FREECAD ASSEMBLY — COMPONENT RECIPES ("surge_platform")

This assembly document has 21 components, labeled P0..P20 below (a component is one placed body or linked part). 10 of them carry a construction recipe — the FreeCAD feature program that regenerates the part from scratch, quoted from this document or its linked companion documents; the rest are supplied as boundary geometry only. No exploded tour is included for this assembly.
COMPONENT P0 — geometry summary ("BK12"; no construction recipe available for this part):
  bounding box: 60.0 x 43.0 x 35.0 mm
  tessellated surface: 281,450 triangles
  volume: 48234 mm^3 (53% of its bounding box)
COMPONENT P1 — geometry summary ("SFU1605_ball_screw_250mm"; no construction recipe available for this part):
  bounding box: 250.0 x 16.0 x 16.0 mm
  tessellated surface: 247,790 triangles
  volume: 33080 mm^3 (52% of its bounding box)
  symmetry: revolution-symmetric about the y axis through its bounding-box center
COMPONENT P2 — geometry summary ("SHF25_001"; no construction recipe available for this part):
  bounding box: 70.0 x 42.0 x 25.0 mm
  tessellated surface: 2,866 triangles
  volume: 24549 mm^3 (33% of its bounding box)
  symmetry: mirror-symmetric across its x mid-plane
COMPONENT P3 — geometry summary ("SHF25_002"; no construction recipe available for this part):
  bounding box: 70.0 x 42.0 x 25.0 mm
  tessellated surface: 2,866 triangles
  volume: 24549 mm^3 (33% of its bounding box)
  symmetry: mirror-symmetric across its x mid-plane
COMPONENT P4 — geometry summary ("SHF25_003"; no construction recipe available for this part):
  bounding box: 70.0 x 42.0 x 25.0 mm
  tessellated surface: 2,866 triangles
  volume: 24549 mm^3 (33% of its bounding box)
  symmetry: mirror-symmetric across its x mid-plane
COMPONENT P5 — geometry summary ("SHF25_000"; no construction recipe available for this part):
  bounding box: 70.0 x 42.0 x 25.0 mm
  tessellated surface: 2,866 triangles
  volume: 24549 mm^3 (33% of its bounding box)
  symmetry: mirror-symmetric across its x mid-plane
COMPONENT P6 — geometry summary ("80ST-M02438"; no construction recipe available for this part):
  bounding box: 185.6 x 92.0 x 80.0 mm
  tessellated surface: 23,724 triangles
  volume: 810178 mm^3 (59% of its bounding box)
COMPONENT P7 — geometry summary ("corner_bracket_40x40_001"; no construction recipe available for this part):
  bounding box: 38.5 x 38.5 x 36.0 mm
  tessellated surface: 328 triangles
  volume: 17428 mm^3 (33% of its bounding box)
  symmetry: mirror-symmetric across its x mid-plane
COMPONENT P8 — geometry summary ("corner_bracket_40x40_002"; no construction recipe available for this part):
  bounding box: 38.5 x 38.5 x 36.0 mm
  tessellated surface: 328 triangles
  volume: 17428 mm^3 (33% of its bounding box)
  symmetry: mirror-symmetric across its x mid-plane
COMPONENT P9 — geometry summary ("corner_bracket_40x40_003"; no construction recipe available for this part):
  bounding box: 38.5 x 38.5 x 36.0 mm
  tessellated surface: 328 triangles
  volume: 17428 mm^3 (33% of its bounding box)
  symmetry: mirror-symmetric across its x mid-plane
COMPONENT P10 — geometry summary ("corner_bracket_40x40_000"; no construction recipe available for this part):
  bounding box: 38.5 x 38.5 x 36.0 mm
  tessellated surface: 328 triangles
  volume: 17428 mm^3 (33% of its bounding box)
  symmetry: mirror-symmetric across its x mid-plane
COMPONENT P11 — recipe-attached ("coupler_10x19", a linked part whose construction recipe lives in a companion FreeCAD document of the same project; that document's serialized recipe follows).
Construction recipe (the companion document, serialized — sketch geometry with constraints, then the solid features built on it; lengths are millimeters unless a unit is written):

FCSTD DOCUMENT  (FreeCAD 1.0R39109 (Git))
Label: coupler
License: All rights reserved
LicenseURL: https://en.wikipedia.org/wiki/All_rights_reserved
objects: Sketcher::SketchObject×3, PartDesign::Pocket×2, PartDesign::Pad×1, PartDesign::Body×1
note: 16 computed .brp shape members not serialized (recipe doc carries the construction recipe); baked Part::Feature solids carry a one-line shape summary decoded from their .brp

FEATURE [Sketcher::SketchObject] Sketch
  ArcFitTolerance = 1e-06
  AttachmentSupport = -> [XZ_Plane]
  FullyConstrained = true
  MakeInternals = false
  MapMode = 5
  Placement = pos=(0,0,0) rot=(1,0,0;1.5708rad)
  sketch-geometry (1):
    g0: Circle CenterX=0 CenterY=0 CenterZ=0 NormalX=0 NormalY=0 NormalZ=1 AngleXU=0 Radius=17.5
  constraints (2):
    c: Coincident(g0,g-1)
    c: Diameter(g0) = 35
FEATURE [PartDesign::Pad] Pad
  Direction = (0,-1,2e-16)
  Length = 50
  Length2 = 10
  Placement = pos=(0,0,0) rot=(1,0,0;1.5708rad)
  Profile = -> Sketch
  ReferenceAxis = -> Sketch [N_Axis]
  Refine = true
  Suppressed = false
  Type = 0
FEATURE [Sketcher::SketchObject] Sketch001
  ArcFitTolerance = 1e-06
  AttachmentSupport = -> [Pad]
  FullyConstrained = true
  MakeInternals = false
  MapMode = 5
  Placement = pos=(0,-50,0) rot=(1,0,0;1.5708rad)
  sketch-geometry (1):
    g0: Circle CenterX=0 CenterY=0 CenterZ=0 NormalX=0 NormalY=0 NormalZ=1 AngleXU=0 Radius=9.5
  constraints (2):
    c: Coincident(g0,g-1)
    c: Diameter(g0) = 19
FEATURE [PartDesign::Pocket] Pocket
  BaseFeature = -> Pad
  Direction = (0,1,-2e-16)
  Length = 18.5
  Length2 = 5
  Placement = pos=(0,0,0) rot=(1,0,0;1.5708rad)
  Profile = -> Sketch001
  ReferenceAxis = -> Sketch001 [N_Axis]
  Refine = true
  Suppressed = false
  Type = 0
FEATURE [Sketcher::SketchObject] Sketch002
  ArcFitTolerance = 1e-06
  AttachmentSupport = -> [Pocket]
  FullyConstrained = true
  MakeInternals = false
  MapMode = 5
  Placement = pos=(0,0,0) rot=(-1,0,0;1.5708rad)
  sketch-geometry (1):
    g0: Circle CenterX=0 CenterY=0 CenterZ=0 NormalX=0 NormalY=0 NormalZ=1 AngleXU=0 Radius=5
  constraints (2):
    c: Diameter(g0) = 10
    c: Coincident(g0,g-1)
FEATURE [PartDesign::Pocket] Pocket001
  BaseFeature = -> Pocket
  Direction = (0,-1,-2e-16)
  Length = 18.5
  Length2 = 5
  Placement = pos=(0,0,0) rot=(1,0,0;1.5708rad)
  Profile = -> Sketch002
  ReferenceAxis = -> Sketch002 [N_Axis]
  Refine = true
  Suppressed = false
  Type = 0
FEATURE [PartDesign::Body] Body  label="coupler_10x19"
  AllowCompound = false
  Group = -> [Sketch,Pad,Sketch001,Pocket,Sketch002,Pocket001]
  Origin = -> Origin
  Tip = -> Pocket001
COMPONENT P12 — recipe-attached ("linear_shaft_25x500_right", a linked part whose construction recipe lives in a companion FreeCAD document of the same project; that document's serialized recipe follows).
Construction recipe (the companion document, serialized — sketch geometry with constraints, then the solid features built on it; lengths are millimeters unless a unit is written):

FCSTD DOCUMENT  (FreeCAD 1.0R39109 (Git))
Label: linear_shaft
License: All rights reserved
LicenseURL: https://en.wikipedia.org/wiki/All_rights_reserved
objects: Sketcher::SketchObject×2, PartDesign::Pad×2, PartDesign::Body×2
note: 12 computed .brp shape members not serialized (recipe doc carries the construction recipe); baked Part::Feature solids carry a one-line shape summary decoded from their .brp

FEATURE [Sketcher::SketchObject] Sketch
  ArcFitTolerance = 1e-06
  AttachmentSupport = -> [XZ_Plane]
  FullyConstrained = true
  MakeInternals = false
  MapMode = 5
  Placement = pos=(0,0,0) rot=(1,0,0;1.5708rad)
  sketch-geometry (1):
    g0: Circle CenterX=0 CenterY=0 CenterZ=0 NormalX=0 NormalY=0 NormalZ=1 AngleXU=0 Radius=12.5
  constraints (2):
    c: Diameter(g0) = 25
    c: Coincident(g0,g-1)
FEATURE [PartDesign::Pad] Pad
  Direction = (0,-1,2e-16)
  Length = 500
  Length2 = 10
  Placement = pos=(0,0,0) rot=(1,0,0;1.5708rad)
  Profile = -> Sketch
  ReferenceAxis = -> Sketch [N_Axis]
  Refine = true
  Suppressed = false
  Type = 0
FEATURE [PartDesign::Body] Body  label="linear_shaft_25x500"
  AllowCompound = false
  Group = -> [Sketch,Pad]
  Origin = -> Origin
  Tip = -> Pad
FEATURE [Sketcher::SketchObject] Sketch001
  ArcFitTolerance = 1e-06
  AttachmentSupport = -> [XZ_Plane001]
  FullyConstrained = true
  MakeInternals = false
  MapMode = 5
  Placement = pos=(0,0,0) rot=(1,0,0;1.5708rad)
  sketch-geometry (1):
    g0: Circle CenterX=0 CenterY=0 CenterZ=0 NormalX=0 NormalY=0 NormalZ=1 AngleXU=0 Radius=12.5
  constraints (2):
    c: Diameter(g0) = 25
    c: Coincident(g0,g-1)
FEATURE [PartDesign::Pad] Pad001
  Direction = (0,-1,2e-16)
  Length = 428
  Length2 = 10
  Placement = pos=(0,0,0) rot=(1,0,0;1.5708rad)
  Profile = -> Sketch001
  ReferenceAxis = -> Sketch001 [N_Axis]
  Refine = true
  Suppressed = false
  Type = 0
FEATURE [PartDesign::Body] Body001  label="linear_shaft_25x428"
  AllowCompound = false
  Group = -> [Sketch001,Pad001]
  Origin = -> Origin001
  Tip = -> Pad001
COMPONENT P13 — same part as P12; its construction recipe is shown at P12.
COMPONENT P14 — recipe-attached ("profile_40x40x500_right", a linked part whose construction recipe lives in a companion FreeCAD document of the same project; that document's serialized recipe follows).
Construction recipe (the companion document, serialized — sketch geometry with constraints, then the solid features built on it; lengths are millimeters unless a unit is written):

FCSTD DOCUMENT  (FreeCAD 1.0R39109 (Git))
Label: profile_40_serie
License: All rights reserved
LicenseURL: https://en.wikipedia.org/wiki/All_rights_reserved
objects: PartDesign::FeatureBase×6, PartDesign::Body×6, PartDesign::Pad×4, Part::Feature×3, PartDesign::Pocket×2
note: 39 computed .brp shape members not serialized (recipe doc carries the construction recipe); baked Part::Feature solids carry a one-line shape summary decoded from their .brp

FEATURE [Part::Feature] Part__Feature  label="profile_40x160x1000"
  shape: bbox 160 x 40 x 1000 mm, 262 faces (baked)
FEATURE [Part::Feature] Part__Feature003  label="profile_40x40x300"
  shape: bbox 40 x 40 x 300 mm, 147 faces (baked)
FEATURE [PartDesign::FeatureBase] BaseFeature
  BaseFeature = -> Part__Feature003
  Suppressed = false
FEATURE [PartDesign::Pad] Pad
  BaseFeature = -> BaseFeature
  Direction = (0,0,1)
  Length = 10
  Length2 = 10
  Profile = -> BaseFeature [Face147]
  Refine = true
  Suppressed = false
  Type = 0
FEATURE [PartDesign::Body] Body  label="profile_40x40x310"
  AllowCompound = false
  BaseFeature = -> Part__Feature003
  Group = -> [BaseFeature,Pad]
  Origin = -> Origin
  Tip = -> Pad
FEATURE [PartDesign::FeatureBase] BaseFeature001
  BaseFeature = -> Part__Feature
  Suppressed = false
FEATURE [PartDesign::Pad] Pad001
  BaseFeature = -> BaseFeature001
  Direction = (0,0,1)
  Length = 350
  Length2 = 10
  Profile = -> BaseFeature001 [Face9]
  Refine = true
  Suppressed = false
  Type = 0
FEATURE [PartDesign::Body] Body001  label="profile_40x160x1350"
  AllowCompound = false
  BaseFeature = -> Part__Feature
  Group = -> [BaseFeature001,Pad001]
  Origin = -> Origin001
  Tip = -> Pad001
FEATURE [PartDesign::FeatureBase] BaseFeature002
  BaseFeature = -> Part__Feature
  Suppressed = false
FEATURE [PartDesign::Pocket] Pocket
  BaseFeature = -> BaseFeature002
  Direction = (0,0,-1)
  Length = 500
  Length2 = 5
  Profile = -> BaseFeature002 [Face9]
  Refine = true
  Suppressed = false
  Type = 0
FEATURE [PartDesign::Body] Body002  label="profile_40x160x500"
  AllowCompound = false
  BaseFeature = -> Part__Feature
  Group = -> [BaseFeature002,Pocket]
  Origin = -> Origin002
  Tip = -> Pocket
FEATURE [PartDesign::FeatureBase] BaseFeature003
  BaseFeature = -> Part__Feature003
  Suppressed = false
FEATURE [PartDesign::Pad] Pad002
  BaseFeature = -> BaseFeature003
  Direction = (0,0,1)
  Length = 200
  Length2 = 10
  Profile = -> BaseFeature003 [Face147]
  Refine = true
  Suppressed = false
  Type = 0
FEATURE [PartDesign::Body] Body003  label="profile_40x40x500"
  AllowCompound = false
  BaseFeature = -> Part__Feature003
  Group = -> [BaseFeature003,Pad002]
  Origin = -> Origin003
  Tip = -> Pad002
FEATURE [Part::Feature] Part__Feature004  label="profile_40x120x80"
  shape: bbox 80 x 120 x 40 mm, 396 faces (baked)
FEATURE [PartDesign::FeatureBase] BaseFeature004
  BaseFeature = -> Part__Feature004
  Suppressed = false
FEATURE [PartDesign::Pad] Pad003
  BaseFeature = -> BaseFeature004
  Direction = (1,0,0)
  Length = 700
  Length2 = 10
  Profile = -> BaseFeature004 [Face396]
  Refine = true
  Suppressed = false
  Type = 0
FEATURE [PartDesign::Body] Body004  label="profile_40x120x780"
  AllowCompound = false
  BaseFeature = -> Part__Feature004
  Group = -> [BaseFeature004,Pad003]
  Origin = -> Origin004
  Tip = -> Pad003
FEATURE [PartDesign::FeatureBase] BaseFeature005
  BaseFeature = -> Part__Feature003
  Suppressed = false
FEATURE [PartDesign::Pocket] Pocket001
  BaseFeature = -> BaseFeature005
  Direction = (0,0,-1)
  Length = 30
  Length2 = 5
  Profile = -> BaseFeature005 [Face147]
  Refine = true
  Suppressed = false
  Type = 0
FEATURE [PartDesign::Body] Body005  label="profile_40x40x270"
  AllowCompound = false
  BaseFeature = -> Part__Feature003
  Group = -> [BaseFeature005,Pocket001]
  Origin = -> Origin005
  Tip = -> Pocket001
COMPONENT P15 — same part as P14; its construction recipe is shown at P14.
COMPONENT P16 — recipe-attached ("surge_BK12_mount_bottom", a linked part whose construction recipe lives in a companion FreeCAD document of the same project; that document's serialized recipe follows).
Construction recipe (the companion document, serialized — sketch geometry with constraints, then the solid features built on it; lengths are millimeters unless a unit is written):

FCSTD DOCUMENT  (FreeCAD 1.0R39109 (Git))
Label: surge_BK12_mount_bottom
License: All rights reserved
LicenseURL: https://en.wikipedia.org/wiki/All_rights_reserved
objects: Sketcher::SketchObject×5, PartDesign::Pocket×4, PartDesign::Fillet×2, PartDesign::Pad×1, PartDesign::Body×1
note: 32 computed .brp shape members not serialized (recipe doc carries the construction recipe); baked Part::Feature solids carry a one-line shape summary decoded from their .brp

FEATURE [Sketcher::SketchObject] Sketch
  ArcFitTolerance = 1e-06
  AttachmentSupport = -> [XZ_Plane]
  FullyConstrained = true
  MakeInternals = false
  MapMode = 5
  Placement = pos=(0,0,0) rot=(1,0,0;1.5708rad)
  sketch-geometry (28):
    g0: LineSegment [constr] StartX=-80 StartY=20 StartZ=0 EndX=-80 EndY=-20 EndZ=0
    g1: LineSegment [constr] StartX=-80 StartY=-20 StartZ=0 EndX=-40 EndY=-20 EndZ=0
    g2: LineSegment [constr] StartX=-40 StartY=-20 StartZ=0 EndX=-40 EndY=20 EndZ=0
    g3: LineSegment [constr] StartX=-40 StartY=20 StartZ=0 EndX=-80 EndY=20 EndZ=0
    g4: LineSegment [constr] StartX=40 StartY=20 StartZ=0 EndX=40 EndY=-20 EndZ=0
    g5: LineSegment [constr] StartX=40 StartY=-20 StartZ=0 EndX=80 EndY=-20 EndZ=0
    g6: LineSegment [constr] StartX=80 StartY=-20 StartZ=0 EndX=80 EndY=20 EndZ=0
    g7: LineSegment [constr] StartX=80 StartY=20 StartZ=0 EndX=40 EndY=20 EndZ=0
    g8: LineSegment [constr] StartX=-40 StartY=-20 StartZ=0 EndX=0 EndY=0 EndZ=0
    g9: LineSegment [constr] StartX=0 StartY=0 StartZ=0 EndX=40 EndY=-20 EndZ=0
    g10: LineSegment [constr] StartX=-30 StartY=-20.5 StartZ=0 EndX=30 EndY=-20.5 EndZ=0
    g11: LineSegment [constr] StartX=30 StartY=-20.5 StartZ=0 EndX=30 EndY=12 EndZ=0
    g12: LineSegment [constr] StartX=-30 StartY=-20.5 StartZ=0 EndX=-30 EndY=12 EndZ=0
    g13: LineSegment [constr] StartX=-30 StartY=12 StartZ=0 EndX=-17 EndY=12 EndZ=0
    g14: LineSegment [constr] StartX=-17 StartY=12 StartZ=0 EndX=-17 EndY=22.5 EndZ=0
    g15: LineSegment [constr] StartX=-17 StartY=22.5 StartZ=0 EndX=17 EndY=22.5 EndZ=0
    g16: LineSegment [constr] StartX=17 StartY=22.5 StartZ=0 EndX=17 EndY=12 EndZ=0
    g17: LineSegment [constr] StartX=17 StartY=12 StartZ=0 EndX=30 EndY=12 EndZ=0
    g18: LineSegment [constr] StartX=-30 StartY=-20.5 StartZ=0 EndX=0 EndY=0 EndZ=0
    g19: LineSegment [constr] StartX=0 StartY=0 StartZ=0 EndX=30 EndY=-20.5 EndZ=0
    g20: LineSegment StartX=-72.5 StartY=-30.4 StartZ=0 EndX=72.5 EndY=-30.4 EndZ=0
    g21: LineSegment StartX=30.4 StartY=-20.9 StartZ=0 EndX=-30.4 EndY=-20.9 EndZ=0
    g22: LineSegment StartX=72.5 StartY=-30.4 StartZ=0 EndX=72.5 EndY=-20.4 EndZ=0
    g23: LineSegment StartX=72.5 StartY=-20.4 StartZ=0 EndX=39.6 EndY=-20.4 EndZ=0
    g24: LineSegment StartX=-72.5 StartY=-30.4 StartZ=0 EndX=-72.5 EndY=-20.4 EndZ=0
    g25: LineSegment StartX=-72.5 StartY=-20.4 StartZ=0 EndX=-39.6 EndY=-20.4 EndZ=0
    g26: LineSegment StartX=-39.6 StartY=-20.4 StartZ=0 EndX=-30.4 EndY=-20.9 EndZ=0
    g27: LineSegment StartX=30.4 StartY=-20.9 StartZ=0 EndX=39.6 EndY=-20.4 EndZ=0
  constraints (80):
    c: Coincident(g0,g1)
    c: Coincident(g1,g2)
    c: Coincident(g2,g3)
    c: Coincident(g3,g0)
    c: Vertical(g0)
    c: Vertical(g2)
    c: Horizontal(g1)
    c: Horizontal(g3)
    c: Coincident(g4,g5)
    c: Coincident(g5,g6)
    c: Coincident(g6,g7)
    c: Coincident(g7,g4)
    c: Vertical(g4)
    c: Vertical(g6)
    c: Horizontal(g5)
    c: Horizontal(g7)
    c: Equal(g4,g7)
    c: Equal(g7,g2)
    c: Equal(g2,g3)
    c: DistanceX(g3,g3) = 40
    c: DistanceX(g2,g4) = 80
    c: DistanceY(g4,g2) = 0
    c: Coincident(g8,g1)
    c: Coincident(g8,g-1)
    c: Coincident(g9,g8)
    c: Coincident(g9,g4)
    c: Equal(g8,g9)
    c: Horizontal(g10)
    c: Coincident(g11,g10)
    c: Vertical(g11)
    c: Coincident(g12,g10)
    c: Vertical(g12)
    c: Coincident(g13,g12)
    c: Horizontal(g13)
    c: Coincident(g14,g13)
    c: Vertical(g14)
    c: Coincident(g15,g14)
    c: Horizontal(g15)
    c: Vertical(g16)
    c: Coincident(g17,g16)
    c: Coincident(g17,g11)
    c: DistanceX(g10,g10) = 60
    c: DistanceY(g12,g12) = 32.5
    c: Coincident(g16,g15)
    c: Horizontal(g17)
    c: Equal(g12,g11)
    c: Equal(g13,g17)
    c: DistanceX(g13,g13) = 13
    c: DistanceY(g14,g14) = 10.5
    c: DistanceY(g12,g2) = 8
    c: Coincident(g18,g10)
    c: Coincident(g18,g8)
    c: Coincident(g19,g8)
    c: Coincident(g19,g10)
    c: Equal(g19,g18)
    c: DistanceY(g8,g2) = 20
    c: Horizontal(g20)
    c: Horizontal(g21)
    c: DistanceY(g21,g10) = 0.4
    c: DistanceX(g21,g10) = 0.4
    c: DistanceX(g10,g21) = 0.4
    c: Coincident(g20,g22)
    c: Vertical(g22)
    c: Coincident(g22,g23)
    c: Horizontal(g23)
    c: Coincident(g20,g24)
    c: Vertical(g24)
    c: Coincident(g24,g25)
    c: Horizontal(g25)
    c: DistanceY(g24,g0) = 0.4
    c: DistanceY(g24,g24) = 10
    c: DistanceX(g1,g25) = 0.4
    c: Equal(g24,g22)
    c: DistanceX(g0,g24) = 7.5
    c: DistanceX(g23,g4) = 0.4
    c: Coincident(g26,g25)
    c: Coincident(g26,g21)
    c: Coincident(g27,g21)
    c: Coincident(g27,g23)
    c: DistanceX(g20,g20) = 145
FEATURE [PartDesign::Pad] Pad
  Direction = (0,-1,2e-16)
  Length = 25
  Length2 = 10
  Placement = pos=(0,0,0) rot=(1,0,0;1.5708rad)
  Profile = -> Sketch
  ReferenceAxis = -> Sketch [N_Axis]
  Refine = true
  Suppressed = false
  Type = 0
FEATURE [Sketcher::SketchObject] Sketch001
  ArcFitTolerance = 1e-06
  AttachmentSupport = -> [Pad]
  FullyConstrained = true
  MakeInternals = false
  MapMode = 5
  Placement = pos=(0,-4.5e-15,-20.4) rot=(0,0,1;3.14159rad)
  sketch-geometry (14):
    g0: LineSegment [constr] StartX=-80 StartY=0 StartZ=0 EndX=-40 EndY=0 EndZ=0
    g1: LineSegment [constr] StartX=-40 StartY=0 StartZ=0 EndX=-40 EndY=25 EndZ=0
    g2: LineSegment [constr] StartX=-40 StartY=25 StartZ=0 EndX=-80 EndY=25 EndZ=0
    g3: LineSegment [constr] StartX=-80 StartY=25 StartZ=0 EndX=-80 EndY=0 EndZ=0
    g4: LineSegment [constr] StartX=80 StartY=0 StartZ=0 EndX=80 EndY=25 EndZ=0
    g5: LineSegment [constr] StartX=80 StartY=25 StartZ=0 EndX=40 EndY=25 EndZ=0
    g6: LineSegment [constr] StartX=40 StartY=25 StartZ=0 EndX=40 EndY=0 EndZ=0
    g7: LineSegment [constr] StartX=40 StartY=0 StartZ=0 EndX=80 EndY=0 EndZ=0
    g8: LineSegment [constr] StartX=-80 StartY=0 StartZ=0 EndX=-40 EndY=25 EndZ=0
    g9: LineSegment [constr] StartX=-40 StartY=0 StartZ=0 EndX=-80 EndY=25 EndZ=0
    g10: LineSegment [constr] StartX=40 StartY=0 StartZ=0 EndX=80 EndY=25 EndZ=0
    g11: LineSegment [constr] StartX=40 StartY=25 StartZ=0 EndX=80 EndY=0 EndZ=0
    g12: Circle CenterX=-60 CenterY=12.5 CenterZ=0 NormalX=0 NormalY=0 NormalZ=1 AngleXU=0 Radius=4.3
    g13: Circle CenterX=60 CenterY=12.5 CenterZ=0 NormalX=0 NormalY=0 NormalZ=1 AngleXU=0 Radius=4.3
  constraints (36):
    c: Coincident(g0,g1)
    c: Coincident(g1,g2)
    c: Coincident(g2,g3)
    c: Coincident(g3,g0)
    c: Horizontal(g0)
    c: Horizontal(g2)
    c: Vertical(g1)
    c: Vertical(g3)
    c: Distance(g1,g3) = 40
    c: Distance(g0,g2) = 25
    c: PointOnObject(g0,g-1)
    c: Coincident(g4,g5)
    c: Coincident(g5,g6)
    c: Coincident(g6,g7)
    c: Coincident(g7,g4)
    c: Vertical(g4)
    c: Vertical(g6)
    c: Horizontal(g5)
    c: Horizontal(g7)
    c: PointOnObject(g4,g-1)
    c: Equal(g0,g7)
    c: Equal(g3,g4)
    c: DistanceX(g0,g-1) = 80
    c: DistanceX(g-1,g4) = 80
    c: Coincident(g8,g0)
    c: Coincident(g8,g1)
    c: Coincident(g9,g0)
    c: Coincident(g9,g2)
    c: Coincident(g10,g6)
    c: Coincident(g10,g4)
    c: Coincident(g11,g5)
    c: Coincident(g11,g4)
    c: Symmetric(g9,g9,g12)
    c: Diameter(g12) = 8.6
    c: Symmetric(g10,g10,g13)
    c: Equal(g13,g12)
FEATURE [PartDesign::Pocket] Pocket
  BaseFeature = -> Pad
  Direction = (0,0,-1)
  Length = 5
  Length2 = 5
  Placement = pos=(0,0,0) rot=(1,0,0;1.5708rad)
  Profile = -> Sketch001
  ReferenceAxis = -> Sketch001 [N_Axis]
  Refine = true
  Suppressed = false
  Type = 1
FEATURE [Sketcher::SketchObject] Sketch002
  ArcFitTolerance = 1e-06
  AttachmentSupport = -> [Pocket]
  FullyConstrained = true
  MakeInternals = false
  MapMode = 5
  Placement = pos=(0,-4.6e-15,-20.9) rot=(0,0,1;3.14159rad)
  sketch-geometry (7):
    g0: Circle CenterX=-23 CenterY=6 CenterZ=0 NormalX=0 NormalY=0 NormalZ=1 AngleXU=0 Radius=3.3
    g1: Circle CenterX=-23 CenterY=19 CenterZ=0 NormalX=0 NormalY=0 NormalZ=1 AngleXU=0 Radius=3.3
    g2: Circle CenterX=23 CenterY=19 CenterZ=0 NormalX=0 NormalY=0 NormalZ=1 AngleXU=0 Radius=3.3
    g3: Circle CenterX=23 CenterY=6 CenterZ=0 NormalX=0 NormalY=0 NormalZ=1 AngleXU=0 Radius=3.3
    g4: LineSegment [constr] StartX=-23 StartY=19 StartZ=0 EndX=23 EndY=6 EndZ=0
    g5: LineSegment [constr] StartX=23 StartY=19 StartZ=0 EndX=-23 EndY=6 EndZ=0
    g6: LineSegment [constr] StartX=0 StartY=0 StartZ=0 EndX=0 EndY=12.5 EndZ=0
  constraints (18):
    c: Diameter(g1) = 6.6
    c: Equal(g1,g0)
    c: Equal(g0,g3)
    c: Equal(g3,g2)
    c: DistanceY(g0,g1) = 13
    c: DistanceX(g1,g0) = 0
    c: DistanceY(g1,g2) = 0
    c: DistanceX(g3,g2) = 0
    c: DistanceY(g3,g0) = 0
    c: DistanceX(g1,g2) = 46
    c: Coincident(g4,g1)
    c: Coincident(g4,g3)
    c: Coincident(g5,g2)
    c: Coincident(g5,g0)
    c: Coincident(g6,g-1)
    c: Symmetric(g4,g4,g6)
    c: Vertical(g6)
    c: DistanceY(g6,g6) = 12.5
FEATURE [PartDesign::Pocket] Pocket001
  BaseFeature = -> Pocket
  Direction = (0,0,-1)
  Length = 5
  Length2 = 5
  Placement = pos=(0,0,0) rot=(1,0,0;1.5708rad)
  Profile = -> Sketch002
  ReferenceAxis = -> Sketch002 [N_Axis]
  Refine = true
  Suppressed = false
  Type = 1
FEATURE [PartDesign::Fillet] Fillet
  Base = -> Pocket001 [Edge13,Edge12,Edge20,Edge14]
  BaseFeature = -> Pocket001
  Placement = pos=(0,0,0) rot=(1,0,0;1.5708rad)
  Radius = 4
  Refine = true
  SupportTransform = false
  Suppressed = false
  UseAllEdges = false
FEATURE [PartDesign::Fillet] Fillet001
  Base = -> Fillet [Edge51,Edge52]
  BaseFeature = -> Fillet
  Placement = pos=(0,0,0) rot=(1,0,0;1.5708rad)
  Radius = 2
  Refine = true
  SupportTransform = false
  Suppressed = false
  UseAllEdges = false
FEATURE [Sketcher::SketchObject] Sketch004
  ArcFitTolerance = 1e-06
  AttachmentOffset = pos=(0,0,-10) rot=(0,0,1;0rad)
  AttachmentSupport = -> [Fillet001]
  FullyConstrained = true
  MakeInternals = false
  MapMode = 5
  Placement = pos=(0,-4.5e-15,-30.4) rot=(0,0,1;3.14159rad)
  sketch-geometry (16):
    g0: LineSegment [constr] StartX=-80 StartY=0 StartZ=0 EndX=-40 EndY=0 EndZ=0
    g1: LineSegment [constr] StartX=-40 StartY=0 StartZ=0 EndX=-40 EndY=25 EndZ=0
    g2: LineSegment [constr] StartX=-40 StartY=25 StartZ=0 EndX=-80 EndY=25 EndZ=0
    g3: LineSegment [constr] StartX=-80 StartY=25 StartZ=0 EndX=-80 EndY=0 EndZ=0
    g4: LineSegment [constr] StartX=80 StartY=0 StartZ=0 EndX=80 EndY=25 EndZ=0
    g5: LineSegment [constr] StartX=80 StartY=25 StartZ=0 EndX=40 EndY=25 EndZ=0
    g6: LineSegment [constr] StartX=40 StartY=25 StartZ=0 EndX=40 EndY=0 EndZ=0
    g7: LineSegment [constr] StartX=40 StartY=0 StartZ=0 EndX=80 EndY=0 EndZ=0
    g8: LineSegment [constr] StartX=-80 StartY=0 StartZ=0 EndX=-40 EndY=25 EndZ=0
    g9: LineSegment [constr] StartX=-40 StartY=0 StartZ=0 EndX=-80 EndY=25 EndZ=0
    g10: LineSegment [constr] StartX=40 StartY=0 StartZ=0 EndX=80 EndY=25 EndZ=0
    g11: LineSegment [constr] StartX=40 StartY=25 StartZ=0 EndX=80 EndY=0 EndZ=0
    g12: Circle [constr] CenterX=-60 CenterY=12.5 CenterZ=0 NormalX=0 NormalY=0 NormalZ=1 AngleXU=0 Radius=4.3
    g13: Circle [constr] CenterX=60 CenterY=12.5 CenterZ=0 NormalX=0 NormalY=0 NormalZ=1 AngleXU=0 Radius=4.3
    g14: Circle CenterX=-60 CenterY=12.5 CenterZ=0 NormalX=0 NormalY=0 NormalZ=1 AngleXU=0 Radius=6.75
    g15: Circle CenterX=60 CenterY=12.5 CenterZ=0 NormalX=0 NormalY=0 NormalZ=1 AngleXU=0 Radius=6.75
  constraints (40):
    c: Coincident(g0,g1)
    c: Coincident(g1,g2)
    c: Coincident(g2,g3)
    c: Coincident(g3,g0)
    c: Horizontal(g0)
    c: Horizontal(g2)
    c: Vertical(g1)
    c: Vertical(g3)
    c: Distance(g1,g3) = 40
    c: Distance(g0,g2) = 25
    c: PointOnObject(g0,g-1)
    c: Coincident(g4,g5)
    c: Coincident(g5,g6)
    c: Coincident(g6,g7)
    c: Coincident(g7,g4)
    c: Vertical(g4)
    c: Vertical(g6)
    c: Horizontal(g5)
    c: Horizontal(g7)
    c: PointOnObject(g4,g-1)
    c: Equal(g0,g7)
    c: Equal(g3,g4)
    c: DistanceX(g0,g-1) = 80
    c: DistanceX(g-1,g4) = 80
    c: Coincident(g8,g0)
    c: Coincident(g8,g1)
    c: Coincident(g9,g0)
    c: Coincident(g9,g2)
    c: Coincident(g10,g6)
    c: Coincident(g10,g4)
    c: Coincident(g11,g5)
    c: Coincident(g11,g4)
    c: Symmetric(g9,g9,g12)
    c: Diameter(g12) = 8.6
    c: Symmetric(g10,g10,g13)
    c: Equal(g13,g12)
    c: Diameter(g14) = 13.5
    c: Coincident(g14,g12)
    c: Coincident(g15,g13)
    c: Equal(g15,g14)
FEATURE [PartDesign::Pocket] Pocket003
  BaseFeature = -> Fillet001
  Direction = (0,0,-1)
  Length = 5
  Length2 = 5
  Placement = pos=(0,0,0) rot=(1,0,0;1.5708rad)
  Profile = -> Sketch004
  ReferenceAxis = -> Sketch004 [N_Axis]
  Refine = true
  Reversed = true
  Suppressed = false
  Type = 0
FEATURE [Sketcher::SketchObject] Sketch006
  ArcFitTolerance = 1e-06
  AttachmentOffset = pos=(0,0,-10) rot=(0,0,1;0rad)
  AttachmentSupport = -> [Pocket003]
  FullyConstrained = true
  MakeInternals = false
  MapMode = 5
  Placement = pos=(0,-4.5e-15,-30.4) rot=(0,0,1;3.14159rad)
  expr: Constraints[0] = Sketch002.Constraints[0]
  expr: Constraints[17] = Sketch002.Constraints[17]
  expr: Constraints[4] = Sketch002.Constraints[4]
  expr: Constraints[5] = Sketch002.Constraints[5]
  expr: Constraints[6] = Sketch002.Constraints[6]
  expr: Constraints[7] = Sketch002.Constraints[7]
  expr: Constraints[8] = Sketch002.Constraints[8]
  expr: Constraints[9] = Sketch002.Constraints[9]
  sketch-geometry (35):
    g0: Circle [constr] CenterX=-23 CenterY=6 CenterZ=0 NormalX=0 NormalY=0 NormalZ=1 AngleXU=0 Radius=3.3
    g1: Circle [constr] CenterX=-23 CenterY=19 CenterZ=0 NormalX=0 NormalY=0 NormalZ=1 AngleXU=0 Radius=3.3
    g2: Circle [constr] CenterX=23 CenterY=19 CenterZ=0 NormalX=0 NormalY=0 NormalZ=1 AngleXU=0 Radius=3.3
    g3: Circle [constr] CenterX=23 CenterY=6 CenterZ=0 NormalX=0 NormalY=0 NormalZ=1 AngleXU=0 Radius=3.3
    g4: LineSegment [constr] StartX=-23 StartY=19 StartZ=0 EndX=23 EndY=6 EndZ=0
    g5: LineSegment [constr] StartX=23 StartY=19 StartZ=0 EndX=-23 EndY=6 EndZ=0
    g6: LineSegment [constr] StartX=0 StartY=0 StartZ=0 EndX=0 EndY=12.5 EndZ=0
    g7: LineSegment StartX=-20.0266 StartY=13.85 StartZ=0 EndX=-17.0533 EndY=19 EndZ=0
    g8: LineSegment StartX=-17.0533 StartY=19 StartZ=0 EndX=-20.0266 EndY=24.15 EndZ=0
    g9: LineSegment StartX=-20.0266 StartY=24.15 StartZ=0 EndX=-25.9734 EndY=24.15 EndZ=0
    g10: LineSegment StartX=-25.9734 StartY=24.15 StartZ=0 EndX=-28.9467 EndY=19 EndZ=0
    g11: LineSegment StartX=-28.9467 StartY=19 StartZ=0 EndX=-25.9734 EndY=13.85 EndZ=0
    g12: LineSegment StartX=-25.9734 StartY=13.85 StartZ=0 EndX=-20.0266 EndY=13.85 EndZ=0
    g13: Circle [constr] CenterX=-23 CenterY=19 CenterZ=0 NormalX=0 NormalY=0 NormalZ=1 AngleXU=0 Radius=5.94671
    g14: LineSegment StartX=-20.0266 StartY=0.85 StartZ=0 EndX=-17.0533 EndY=6 EndZ=0
    g15: LineSegment StartX=-17.0533 StartY=6 StartZ=0 EndX=-20.0266 EndY=11.15 EndZ=0
    g16: LineSegment StartX=-20.0266 StartY=11.15 StartZ=0 EndX=-25.9734 EndY=11.15 EndZ=0
    g17: LineSegment StartX=-25.9734 StartY=11.15 StartZ=0 EndX=-28.9467 EndY=6 EndZ=0
    g18: LineSegment StartX=-28.9467 StartY=6 StartZ=0 EndX=-25.9734 EndY=0.85 EndZ=0
    g19: LineSegment StartX=-25.9734 StartY=0.85 StartZ=0 EndX=-20.0266 EndY=0.85 EndZ=0
    g20: Circle [constr] CenterX=-23 CenterY=6 CenterZ=0 NormalX=0 NormalY=0 NormalZ=1 AngleXU=0 Radius=5.94671
    g21: LineSegment StartX=25.9734 StartY=13.85 StartZ=0 EndX=28.9467 EndY=19 EndZ=0
    g22: LineSegment StartX=28.9467 StartY=19 StartZ=0 EndX=25.9734 EndY=24.15 EndZ=0
    g23: LineSegment StartX=25.9734 StartY=24.15 StartZ=0 EndX=20.0266 EndY=24.15 EndZ=0
    g24: LineSegment StartX=20.0266 StartY=24.15 StartZ=0 EndX=17.0533 EndY=19 EndZ=0
    g25: LineSegment StartX=17.0533 StartY=19 StartZ=0 EndX=20.0266 EndY=13.85 EndZ=0
    g26: LineSegment StartX=20.0266 StartY=13.85 StartZ=0 EndX=25.9734 EndY=13.85 EndZ=0
    g27: Circle [constr] CenterX=23 CenterY=19 CenterZ=0 NormalX=0 NormalY=0 NormalZ=1 AngleXU=0 Radius=5.94671
    g28: LineSegment StartX=25.9734 StartY=0.85 StartZ=0 EndX=28.9467 EndY=6 EndZ=0
    g29: LineSegment StartX=28.9467 StartY=6 StartZ=0 EndX=25.9734 EndY=11.15 EndZ=0
    g30: LineSegment StartX=25.9734 StartY=11.15 StartZ=0 EndX=20.0266 EndY=11.15 EndZ=0
    g31: LineSegment StartX=20.0266 StartY=11.15 StartZ=0 EndX=17.0533 EndY=6 EndZ=0
    g32: LineSegment StartX=17.0533 StartY=6 StartZ=0 EndX=20.0266 EndY=0.85 EndZ=0
    g33: LineSegment StartX=20.0266 StartY=0.85 StartZ=0 EndX=25.9734 EndY=0.85 EndZ=0
    g34: Circle [constr] CenterX=23 CenterY=6 CenterZ=0 NormalX=0 NormalY=0 NormalZ=1 AngleXU=0 Radius=5.94671
  constraints (82):
    c: Diameter(g1) = 6.6
    c: Equal(g1,g0)
    c: Equal(g0,g3)
    c: Equal(g3,g2)
    c: DistanceY(g0,g1) = 13
    c: DistanceX(g1,g0) = 0
    c: DistanceY(g1,g2) = 0
    c: DistanceX(g3,g2) = 0
    c: DistanceY(g3,g0) = 0
    c: DistanceX(g1,g2) = 46
    c: Coincident(g4,g1)
    c: Coincident(g4,g3)
    c: Coincident(g5,g2)
    c: Coincident(g5,g0)
    c: Coincident(g6,g-1)
    c: Symmetric(g4,g4,g6)
    c: Vertical(g6)
    c: DistanceY(g6,g6) = 12.5
    c: Coincident(g7,g8)
    c: Coincident(g8,g9)
    c: Coincident(g9,g10)
    c: Coincident(g10,g11)
    c: Coincident(g11,g12)
    c: Coincident(g12,g7)
    c: Equal(g7, g8-g12) x5
    c: PointOnObject(g7,g13)
    c: PointOnObject(g8,g13)
    c: PointOnObject(g9,g13)
    c: PointOnObject(g10,g13)
    c: PointOnObject(g11,g13)
    c: PointOnObject(g12,g13)
    c: Coincident(g13,g1)
    c: Coincident(g14,g15)
    c: Coincident(g15,g16)
    c: Coincident(g16,g17)
    c: Coincident(g17,g18)
    c: Coincident(g18,g19)
    c: Coincident(g19,g14)
    c: Equal(g14, g15-g19) x5
    c: PointOnObject(g14,g20)
    c: PointOnObject(g15,g20)
    c: PointOnObject(g16,g20)
    c: PointOnObject(g17,g20)
    c: PointOnObject(g18,g20)
    c: PointOnObject(g19,g20)
    c: Coincident(g20,g0)
    c: Coincident(g21,g22)
    c: Coincident(g22,g23)
    c: Coincident(g23,g24)
    c: Coincident(g24,g25)
    c: Coincident(g25,g26)
    c: Coincident(g26,g21)
    c: Equal(g21, g22-g26) x5
    c: PointOnObject(g21,g27)
    c: PointOnObject(g22,g27)
    c: PointOnObject(g23,g27)
    c: PointOnObject(g24,g27)
    c: PointOnObject(g25,g27)
    c: PointOnObject(g26,g27)
    c: Coincident(g27,g2)
    c: Coincident(g28,g29)
    c: Coincident(g29,g30)
    c: Coincident(g30,g31)
    c: Coincident(g31,g32)
    c: Coincident(g32,g33)
    c: Coincident(g33,g28)
    c: Equal(g28, g29-g33) x5
    c: PointOnObject(g28,g34)
    c: PointOnObject(g29,g34)
    c: PointOnObject(g30,g34)
    c: PointOnObject(g31,g34)
    c: PointOnObject(g32,g34)
    c: PointOnObject(g33,g34)
    c: Coincident(g34,g3)
    c: Horizontal(g9)
    c: Horizontal(g16)
    c: Horizontal(g23)
    c: Horizontal(g30)
    c: Distance(g9,g7) = 10.3
    c: Equal(g13,g20)
    c: Equal(g20,g34)
    c: Equal(g34,g27)
FEATURE [PartDesign::Pocket] Pocket005
  BaseFeature = -> Pocket003
  Direction = (0,0,-1)
  Length = 4
  Length2 = 5
  Placement = pos=(0,0,0) rot=(1,0,0;1.5708rad)
  Profile = -> Sketch006
  ReferenceAxis = -> Sketch006 [N_Axis]
  Refine = true
  Reversed = true
  Suppressed = false
  Type = 0
FEATURE [PartDesign::Body] Body  label="surge_BK12_mount_bottom"
  AllowCompound = false
  Group = -> [Sketch,Pad,Sketch001,Pocket,Sketch002,Pocket001,Fillet,Fillet001,Sketch004,Pocket003,Sketch006,Pocket005]
  Origin = -> Origin
  Tip = -> Pocket005
COMPONENT P17 — recipe-attached ("surge_BK12_mount_top", a linked part whose construction recipe lives in a companion FreeCAD document of the same project; that document's serialized recipe follows).
Construction recipe (the companion document, serialized — sketch geometry with constraints, then the solid features built on it; lengths are millimeters unless a unit is written):

FCSTD DOCUMENT  (FreeCAD 1.0R39109 (Git))
Label: surge_BK12_mount_top
License: All rights reserved
LicenseURL: https://en.wikipedia.org/wiki/All_rights_reserved
objects: Sketcher::SketchObject×5, PartDesign::Pocket×4, PartDesign::Fillet×2, PartDesign::Pad×1, PartDesign::Body×1
note: 32 computed .brp shape members not serialized (recipe doc carries the construction recipe); baked Part::Feature solids carry a one-line shape summary decoded from their .brp

FEATURE [Sketcher::SketchObject] Sketch
  ArcFitTolerance = 1e-06
  AttachmentSupport = -> [XZ_Plane]
  FullyConstrained = true
  MakeInternals = false
  MapMode = 5
  Placement = pos=(0,0,0) rot=(1,0,0;1.5708rad)
  sketch-geometry (32):
    g0: LineSegment [constr] StartX=-80 StartY=20 StartZ=0 EndX=-80 EndY=-20 EndZ=0
    g1: LineSegment [constr] StartX=-80 StartY=-20 StartZ=0 EndX=-40 EndY=-20 EndZ=0
    g2: LineSegment [constr] StartX=-40 StartY=-20 StartZ=0 EndX=-40 EndY=20 EndZ=0
    g3: LineSegment [constr] StartX=-40 StartY=20 StartZ=0 EndX=-80 EndY=20 EndZ=0
    g4: LineSegment [constr] StartX=40 StartY=20 StartZ=0 EndX=40 EndY=-20 EndZ=0
    g5: LineSegment [constr] StartX=40 StartY=-20 StartZ=0 EndX=80 EndY=-20 EndZ=0
    g6: LineSegment [constr] StartX=80 StartY=-20 StartZ=0 EndX=80 EndY=20 EndZ=0
    g7: LineSegment [constr] StartX=80 StartY=20 StartZ=0 EndX=40 EndY=20 EndZ=0
    g8: LineSegment [constr] StartX=-40 StartY=-20 StartZ=0 EndX=0 EndY=0 EndZ=0
    g9: LineSegment [constr] StartX=0 StartY=0 StartZ=0 EndX=40 EndY=-20 EndZ=0
    g10: LineSegment [constr] StartX=-30 StartY=-20.5 StartZ=0 EndX=30 EndY=-20.5 EndZ=0
    g11: LineSegment [constr] StartX=30 StartY=-20.5 StartZ=0 EndX=30 EndY=12 EndZ=0
    g12: LineSegment [constr] StartX=-30 StartY=-20.5 StartZ=0 EndX=-30 EndY=12 EndZ=0
    g13: LineSegment [constr] StartX=-30 StartY=12 StartZ=0 EndX=-17 EndY=12 EndZ=0
    g14: LineSegment [constr] StartX=-17 StartY=12 StartZ=0 EndX=-17 EndY=22.5 EndZ=0
    g15: LineSegment [constr] StartX=-17 StartY=22.5 StartZ=0 EndX=17 EndY=22.5 EndZ=0
    g16: LineSegment [constr] StartX=17 StartY=22.5 StartZ=0 EndX=17 EndY=12 EndZ=0
    g17: LineSegment [constr] StartX=17 StartY=12 StartZ=0 EndX=30 EndY=12 EndZ=0
    g18: LineSegment [constr] StartX=-30 StartY=-20.5 StartZ=0 EndX=0 EndY=0 EndZ=0
    g19: LineSegment [constr] StartX=0 StartY=0 StartZ=0 EndX=30 EndY=-20.5 EndZ=0
    g20: LineSegment StartX=72.5 StartY=30.4 StartZ=0 EndX=-72.5 EndY=30.4 EndZ=0
    g21: LineSegment StartX=-30 StartY=12.4 StartZ=0 EndX=-17.4 EndY=12.4 EndZ=0
    g22: LineSegment StartX=-17.4 StartY=12.4 StartZ=0 EndX=-17.4 EndY=22.9 EndZ=0
    g23: LineSegment StartX=-17.4 StartY=22.9 StartZ=0 EndX=17.4 EndY=22.9 EndZ=0
    g24: LineSegment StartX=17.4 StartY=22.9 StartZ=0 EndX=17.4 EndY=12.4 EndZ=0
    g25: LineSegment StartX=17.4 StartY=12.4 StartZ=0 EndX=30 EndY=12.4 EndZ=0
    g26: LineSegment StartX=39.6 StartY=20.4 StartZ=0 EndX=72.5 EndY=20.4 EndZ=0
    g27: LineSegment StartX=72.5 StartY=20.4 StartZ=0 EndX=72.5 EndY=30.4 EndZ=0
    g28: LineSegment StartX=-39.6 StartY=20.4 StartZ=0 EndX=-72.5 EndY=20.4 EndZ=0
    g29: LineSegment StartX=-72.5 StartY=20.4 StartZ=0 EndX=-72.5 EndY=30.4 EndZ=0
    g30: LineSegment StartX=-39.6 StartY=20.4 StartZ=0 EndX=-30 EndY=12.4 EndZ=0
    g31: LineSegment StartX=30 StartY=12.4 StartZ=0 EndX=39.6 EndY=20.4 EndZ=0
  constraints (92):
    c: Coincident(g0,g1)
    c: Coincident(g1,g2)
    c: Coincident(g2,g3)
    c: Coincident(g3,g0)
    c: Vertical(g0)
    c: Vertical(g2)
    c: Horizontal(g1)
    c: Horizontal(g3)
    c: Coincident(g4,g5)
    c: Coincident(g5,g6)
    c: Coincident(g6,g7)
    c: Coincident(g7,g4)
    c: Vertical(g4)
    c: Vertical(g6)
    c: Horizontal(g5)
    c: Horizontal(g7)
    c: Equal(g4,g7)
    c: Equal(g7,g2)
    c: Equal(g2,g3)
    c: DistanceX(g3,g3) = 40
    c: DistanceX(g2,g4) = 80
    c: DistanceY(g4,g2) = 0
    c: Coincident(g8,g1)
    c: Coincident(g8,g-1)
    c: Coincident(g9,g8)
    c: Coincident(g9,g4)
    c: Equal(g8,g9)
    c: Horizontal(g10)
    c: Coincident(g11,g10)
    c: Vertical(g11)
    c: Coincident(g12,g10)
    c: Vertical(g12)
    c: Coincident(g13,g12)
    c: Horizontal(g13)
    c: Coincident(g14,g13)
    c: Vertical(g14)
    c: Coincident(g15,g14)
    c: Horizontal(g15)
    c: Vertical(g16)
    c: Coincident(g17,g16)
    c: Coincident(g17,g11)
    c: DistanceX(g10,g10) = 60
    c: DistanceY(g12,g12) = 32.5
    c: Coincident(g16,g15)
    c: Horizontal(g17)
    c: Equal(g12,g11)
    c: Equal(g13,g17)
    c: DistanceX(g13,g13) = 13
    c: DistanceY(g14,g14) = 10.5
    c: DistanceY(g12,g2) = 8
    c: Coincident(g18,g10)
    c: Coincident(g18,g8)
    c: Coincident(g19,g8)
    c: Coincident(g19,g10)
    c: Equal(g19,g18)
    c: DistanceY(g8,g2) = 20
    c: Horizontal(g20)
    c: Horizontal(g21)
    c: Coincident(g21,g22)
    c: Vertical(g22)
    c: Coincident(g22,g23)
    c: Horizontal(g23)
    c: Coincident(g23,g24)
    c: Vertical(g24)
    c: Coincident(g24,g25)
    c: Horizontal(g25)
    c: Equal(g21,g25)
    c: DistanceY(g12,g21) = 0.4
    c: DistanceX(g21,g13) = 0.4
    c: DistanceY(g14,g22) = 0.4
    c: Horizontal(g26)
    c: Coincident(g26,g27)
    c: Coincident(g27,g20)
    c: Vertical(g27)
    c: Horizontal(g28)
    c: Coincident(g28,g29)
    c: Coincident(g29,g20)
    c: Vertical(g29)
    c: DistanceY(g2,g28) = 0.4
    c: Equal(g26,g28)
    c: DistanceX(g2,g28) = 0.4
    c: Coincident(g30,g28)
    c: Coincident(g30,g21)
    c: DistanceX(g20,g20) = 145
    c: DistanceY(g29,g29) = 10
    c: Equal(g27,g29)
    c: DistanceX(g26,g4) = 0.4
    c: Coincident(g31,g25)
    c: Coincident(g31,g26)
    c: DistanceX(g21,g12) = 0
    c: DistanceX(g15,g23) = 0.4
    c: Equal(g24,g22)
FEATURE [PartDesign::Pad] Pad
  Direction = (0,-1,2e-16)
  Length = 25
  Length2 = 10
  Placement = pos=(0,0,0) rot=(1,0,0;1.5708rad)
  Profile = -> Sketch
  ReferenceAxis = -> Sketch [N_Axis]
  Refine = true
  Suppressed = false
  Type = 0
FEATURE [Sketcher::SketchObject] Sketch001
  ArcFitTolerance = 1e-06
  AttachmentSupport = -> [Pad]
  FullyConstrained = true
  MakeInternals = false
  MapMode = 5
  Placement = pos=(0,6.8e-15,30.4) rot=(0,0,1;3.14159rad)
  sketch-geometry (14):
    g0: LineSegment [constr] StartX=-80 StartY=0 StartZ=0 EndX=-40 EndY=0 EndZ=0
    g1: LineSegment [constr] StartX=-40 StartY=0 StartZ=0 EndX=-40 EndY=25 EndZ=0
    g2: LineSegment [constr] StartX=-40 StartY=25 StartZ=0 EndX=-80 EndY=25 EndZ=0
    g3: LineSegment [constr] StartX=-80 StartY=25 StartZ=0 EndX=-80 EndY=0 EndZ=0
    g4: LineSegment [constr] StartX=80 StartY=0 StartZ=0 EndX=80 EndY=25 EndZ=0
    g5: LineSegment [constr] StartX=80 StartY=25 StartZ=0 EndX=40 EndY=25 EndZ=0
    g6: LineSegment [constr] StartX=40 StartY=25 StartZ=0 EndX=40 EndY=0 EndZ=0
    g7: LineSegment [constr] StartX=40 StartY=0 StartZ=0 EndX=80 EndY=0 EndZ=0
    g8: LineSegment [constr] StartX=-80 StartY=0 StartZ=0 EndX=-40 EndY=25 EndZ=0
    g9: LineSegment [constr] StartX=-40 StartY=0 StartZ=0 EndX=-80 EndY=25 EndZ=0
    g10: LineSegment [constr] StartX=40 StartY=0 StartZ=0 EndX=80 EndY=25 EndZ=0
    g11: LineSegment [constr] StartX=40 StartY=25 StartZ=0 EndX=80 EndY=0 EndZ=0
    g12: Circle CenterX=-60 CenterY=12.5 CenterZ=0 NormalX=0 NormalY=0 NormalZ=1 AngleXU=0 Radius=4.3
    g13: Circle CenterX=60 CenterY=12.5 CenterZ=0 NormalX=0 NormalY=0 NormalZ=1 AngleXU=0 Radius=4.3
  constraints (36):
    c: Coincident(g0,g1)
    c: Coincident(g1,g2)
    c: Coincident(g2,g3)
    c: Coincident(g3,g0)
    c: Horizontal(g0)
    c: Horizontal(g2)
    c: Vertical(g1)
    c: Vertical(g3)
    c: Distance(g1,g3) = 40
    c: Distance(g0,g2) = 25
    c: PointOnObject(g0,g-1)
    c: Coincident(g4,g5)
    c: Coincident(g5,g6)
    c: Coincident(g6,g7)
    c: Coincident(g7,g4)
    c: Vertical(g4)
    c: Vertical(g6)
    c: Horizontal(g5)
    c: Horizontal(g7)
    c: PointOnObject(g4,g-1)
    c: Equal(g0,g7)
    c: Equal(g3,g4)
    c: DistanceX(g0,g-1) = 80
    c: DistanceX(g-1,g4) = 80
    c: Coincident(g8,g0)
    c: Coincident(g8,g1)
    c: Coincident(g9,g0)
    c: Coincident(g9,g2)
    c: Coincident(g10,g6)
    c: Coincident(g10,g4)
    c: Coincident(g11,g5)
    c: Coincident(g11,g4)
    c: Symmetric(g9,g9,g12)
    c: Diameter(g12) = 8.6
    c: Symmetric(g10,g10,g13)
    c: Equal(g13,g12)
FEATURE [PartDesign::Pocket] Pocket
  BaseFeature = -> Pad
  Direction = (0,0,-1)
  Length = 5
  Length2 = 5
  Placement = pos=(0,0,0) rot=(1,0,0;1.5708rad)
  Profile = -> Sketch001
  ReferenceAxis = -> Sketch001 [N_Axis]
  Refine = true
  Suppressed = false
  Type = 1
FEATURE [Sketcher::SketchObject] Sketch002
  ArcFitTolerance = 1e-06
  AttachmentSupport = -> [Pocket]
  FullyConstrained = true
  MakeInternals = false
  MapMode = 5
  Placement = pos=(0,6.8e-15,30.4) rot=(0,0,1;3.14159rad)
  sketch-geometry (7):
    g0: Circle CenterX=-23 CenterY=6 CenterZ=0 NormalX=0 NormalY=0 NormalZ=1 AngleXU=0 Radius=3.3
    g1: Circle CenterX=-23 CenterY=19 CenterZ=0 NormalX=0 NormalY=0 NormalZ=1 AngleXU=0 Radius=3.3
    g2: Circle CenterX=23 CenterY=19 CenterZ=0 NormalX=0 NormalY=0 NormalZ=1 AngleXU=0 Radius=3.3
    g3: Circle CenterX=23 CenterY=6 CenterZ=0 NormalX=0 NormalY=0 NormalZ=1 AngleXU=0 Radius=3.3
    g4: LineSegment [constr] StartX=-23 StartY=19 StartZ=0 EndX=23 EndY=6 EndZ=0
    g5: LineSegment [constr] StartX=23 StartY=19 StartZ=0 EndX=-23 EndY=6 EndZ=0
    g6: LineSegment [constr] StartX=0 StartY=0 StartZ=0 EndX=0 EndY=12.5 EndZ=0
  constraints (18):
    c: Diameter(g1) = 6.6
    c: Equal(g1,g0)
    c: Equal(g0,g3)
    c: Equal(g3,g2)
    c: DistanceY(g0,g1) = 13
    c: DistanceX(g1,g0) = 0
    c: DistanceY(g1,g2) = 0
    c: DistanceX(g3,g2) = 0
    c: DistanceY(g3,g0) = 0
    c: DistanceX(g1,g2) = 46
    c: Coincident(g4,g1)
    c: Coincident(g4,g3)
    c: Coincident(g5,g2)
    c: Coincident(g5,g0)
    c: Coincident(g6,g-1)
    c: Symmetric(g4,g4,g6)
    c: Vertical(g6)
    c: DistanceY(g6,g6) = 12.5
FEATURE [PartDesign::Pocket] Pocket001
  BaseFeature = -> Pocket
  Direction = (0,0,-1)
  Length = 5
  Length2 = 5
  Placement = pos=(0,0,0) rot=(1,0,0;1.5708rad)
  Profile = -> Sketch002
  ReferenceAxis = -> Sketch002 [N_Axis]
  Refine = true
  Suppressed = false
  Type = 1
FEATURE [PartDesign::Fillet] Fillet
  Base = -> Pocket001 [Edge31,Edge22,Edge29,Edge20]
  BaseFeature = -> Pocket001
  Placement = pos=(0,0,0) rot=(1,0,0;1.5708rad)
  Radius = 4
  Refine = true
  SupportTransform = false
  Suppressed = false
  UseAllEdges = false
FEATURE [PartDesign::Fillet] Fillet001
  Base = -> Fillet [Edge39,Edge3]
  BaseFeature = -> Fillet
  Placement = pos=(0,0,0) rot=(1,0,0;1.5708rad)
  Radius = 2
  Refine = true
  SupportTransform = false
  Suppressed = false
  UseAllEdges = false
FEATURE [Sketcher::SketchObject] Sketch003
  ArcFitTolerance = 1e-06
  AttachmentSupport = -> [Fillet001]
  FullyConstrained = true
  MakeInternals = false
  MapMode = 5
  Placement = pos=(0,6.8e-15,30.4) rot=(0,0,1;3.14159rad)
  expr: Constraints[22] = Sketch001.Constraints[22]
  expr: Constraints[23] = Sketch001.Constraints[23]
  expr: Constraints[33] = Sketch001.Constraints[33]
  expr: Constraints[8] = Sketch001.Constraints[8]
  expr: Constraints[9] = Sketch001.Constraints[9]
  sketch-geometry (16):
    g0: LineSegment [constr] StartX=-80 StartY=0 StartZ=0 EndX=-40 EndY=0 EndZ=0
    g1: LineSegment [constr] StartX=-40 StartY=0 StartZ=0 EndX=-40 EndY=25 EndZ=0
    g2: LineSegment [constr] StartX=-40 StartY=25 StartZ=0 EndX=-80 EndY=25 EndZ=0
    g3: LineSegment [constr] StartX=-80 StartY=25 StartZ=0 EndX=-80 EndY=0 EndZ=0
    g4: LineSegment [constr] StartX=80 StartY=0 StartZ=0 EndX=80 EndY=25 EndZ=0
    g5: LineSegment [constr] StartX=80 StartY=25 StartZ=0 EndX=40 EndY=25 EndZ=0
    g6: LineSegment [constr] StartX=40 StartY=25 StartZ=0 EndX=40 EndY=0 EndZ=0
    g7: LineSegment [constr] StartX=40 StartY=0 StartZ=0 EndX=80 EndY=0 EndZ=0
    g8: LineSegment [constr] StartX=-80 StartY=0 StartZ=0 EndX=-40 EndY=25 EndZ=0
    g9: LineSegment [constr] StartX=-40 StartY=0 StartZ=0 EndX=-80 EndY=25 EndZ=0
    g10: LineSegment [constr] StartX=40 StartY=0 StartZ=0 EndX=80 EndY=25 EndZ=0
    g11: LineSegment [constr] StartX=40 StartY=25 StartZ=0 EndX=80 EndY=0 EndZ=0
    g12: Circle [constr] CenterX=-60 CenterY=12.5 CenterZ=0 NormalX=0 NormalY=0 NormalZ=1 AngleXU=0 Radius=4.3
    g13: Circle [constr] CenterX=60 CenterY=12.5 CenterZ=0 NormalX=0 NormalY=0 NormalZ=1 AngleXU=0 Radius=4.3
    g14: Circle CenterX=-60 CenterY=12.5 CenterZ=0 NormalX=0 NormalY=0 NormalZ=1 AngleXU=0 Radius=6.75
    g15: Circle CenterX=60 CenterY=12.5 CenterZ=0 NormalX=0 NormalY=0 NormalZ=1 AngleXU=0 Radius=6.75
  constraints (40):
    c: Coincident(g0,g1)
    c: Coincident(g1,g2)
    c: Coincident(g2,g3)
    c: Coincident(g3,g0)
    c: Horizontal(g0)
    c: Horizontal(g2)
    c: Vertical(g1)
    c: Vertical(g3)
    c: Distance(g1,g3) = 40
    c: Distance(g0,g2) = 25
    c: PointOnObject(g0,g-1)
    c: Coincident(g4,g5)
    c: Coincident(g5,g6)
    c: Coincident(g6,g7)
    c: Coincident(g7,g4)
    c: Vertical(g4)
    c: Vertical(g6)
    c: Horizontal(g5)
    c: Horizontal(g7)
    c: PointOnObject(g4,g-1)
    c: Equal(g0,g7)
    c: Equal(g3,g4)
    c: DistanceX(g0,g-1) = 80
    c: DistanceX(g-1,g4) = 80
    c: Coincident(g8,g0)
    c: Coincident(g8,g1)
    c: Coincident(g9,g0)
    c: Coincident(g9,g2)
    c: Coincident(g10,g6)
    c: Coincident(g10,g4)
    c: Coincident(g11,g5)
    c: Coincident(g11,g4)
    c: Symmetric(g9,g9,g12)
    c: Diameter(g12) = 8.6
    c: Symmetric(g10,g10,g13)
    c: Equal(g13,g12)
    c: Diameter(g14) = 13.5
    c: Coincident(g14,g12)
    c: Coincident(g15,g13)
    c: Equal(g15,g14)
FEATURE [PartDesign::Pocket] Pocket002
  BaseFeature = -> Fillet001
  Direction = (0,0,-1)
  Length = 5
  Length2 = 5
  Placement = pos=(0,0,0) rot=(1,0,0;1.5708rad)
  Profile = -> Sketch003
  ReferenceAxis = -> Sketch003 [N_Axis]
  Refine = true
  Suppressed = false
  Type = 0
FEATURE [Sketcher::SketchObject] Sketch005
  ArcFitTolerance = 1e-06
  AttachmentSupport = -> [Pocket002]
  FullyConstrained = true
  MakeInternals = false
  MapMode = 5
  Placement = pos=(0,6.8e-15,30.4) rot=(0,0,1;3.14159rad)
  expr: Constraints[0] = Sketch002.Constraints[0]
  expr: Constraints[17] = Sketch002.Constraints[17]
  expr: Constraints[4] = Sketch002.Constraints[4]
  expr: Constraints[5] = Sketch002.Constraints[5]
  expr: Constraints[6] = Sketch002.Constraints[6]
  expr: Constraints[7] = Sketch002.Constraints[7]
  expr: Constraints[8] = Sketch002.Constraints[8]
  expr: Constraints[9] = Sketch002.Constraints[9]
  sketch-geometry (11):
    g0: Circle [constr] CenterX=-23 CenterY=6 CenterZ=0 NormalX=0 NormalY=0 NormalZ=1 AngleXU=0 Radius=3.3
    g1: Circle [constr] CenterX=-23 CenterY=19 CenterZ=0 NormalX=0 NormalY=0 NormalZ=1 AngleXU=0 Radius=3.3
    g2: Circle [constr] CenterX=23 CenterY=19 CenterZ=0 NormalX=0 NormalY=0 NormalZ=1 AngleXU=0 Radius=3.3
    g3: Circle [constr] CenterX=23 CenterY=6 CenterZ=0 NormalX=0 NormalY=0 NormalZ=1 AngleXU=0 Radius=3.3
    g4: LineSegment [constr] StartX=-23 StartY=19 StartZ=0 EndX=23 EndY=6 EndZ=0
    g5: LineSegment [constr] StartX=23 StartY=19 StartZ=0 EndX=-23 EndY=6 EndZ=0
    g6: LineSegment [constr] StartX=0 StartY=0 StartZ=0 EndX=0 EndY=12.5 EndZ=0
    g7: Circle CenterX=-23 CenterY=19 CenterZ=0 NormalX=0 NormalY=0 NormalZ=1 AngleXU=0 Radius=5.25
    g8: Circle CenterX=-23 CenterY=6 CenterZ=0 NormalX=0 NormalY=0 NormalZ=1 AngleXU=0 Radius=5.25
    g9: Circle CenterX=23 CenterY=6 CenterZ=0 NormalX=0 NormalY=0 NormalZ=1 AngleXU=0 Radius=5.25
    g10: Circle CenterX=23 CenterY=19 CenterZ=0 NormalX=0 NormalY=0 NormalZ=1 AngleXU=0 Radius=5.25
  constraints (26):
    c: Diameter(g1) = 6.6
    c: Equal(g1,g0)
    c: Equal(g0,g3)
    c: Equal(g3,g2)
    c: DistanceY(g0,g1) = 13
    c: DistanceX(g1,g0) = 0
    c: DistanceY(g1,g2) = 0
    c: DistanceX(g3,g2) = 0
    c: DistanceY(g3,g0) = 0
    c: DistanceX(g1,g2) = 46
    c: Coincident(g4,g1)
    c: Coincident(g4,g3)
    c: Coincident(g5,g2)
    c: Coincident(g5,g0)
    c: Coincident(g6,g-1)
    c: Symmetric(g4,g4,g6)
    c: Vertical(g6)
    c: DistanceY(g6,g6) = 12.5
    c: Diameter(g7) = 10.5
    c: Coincident(g7,g1)
    c: Coincident(g8,g0)
    c: Coincident(g9,g3)
    c: Coincident(g10,g2)
    c: Equal(g7,g10)
    c: Equal(g10,g9)
    c: Equal(g9,g8)
FEATURE [PartDesign::Pocket] Pocket004
  BaseFeature = -> Pocket002
  Direction = (0,0,-1)
  Length = 5
  Length2 = 5
  Placement = pos=(0,0,0) rot=(1,0,0;1.5708rad)
  Profile = -> Sketch005
  ReferenceAxis = -> Sketch005 [N_Axis]
  Refine = true
  Suppressed = false
  Type = 0
FEATURE [PartDesign::Body] Body  label="surge_BK12_mount_top"
  AllowCompound = false
  Group = -> [Sketch,Pad,Sketch001,Pocket,Sketch002,Pocket001,Fillet,Fillet001,Sketch003,Pocket002,Sketch005,Pocket004]
  Origin = -> Origin
  Tip = -> Pocket004
COMPONENT P18 — recipe-attached ("surge_motor_mount_bottom", a linked part whose construction recipe lives in a companion FreeCAD document of the same project; that document's serialized recipe follows).
Construction recipe (the companion document, serialized — sketch geometry with constraints, then the solid features built on it; lengths are millimeters unless a unit is written):

FCSTD DOCUMENT  (FreeCAD 1.0R39109 (Git))
Label: surge_motor_mount_bottom
License: All rights reserved
LicenseURL: https://en.wikipedia.org/wiki/All_rights_reserved
objects: Sketcher::SketchObject×3, PartDesign::Pocket×2, PartDesign::Fillet×2, PartDesign::Pad×1, PartDesign::Body×1
note: 22 computed .brp shape members not serialized (recipe doc carries the construction recipe); baked Part::Feature solids carry a one-line shape summary decoded from their .brp

FEATURE [Sketcher::SketchObject] Sketch
  ArcFitTolerance = 1e-06
  AttachmentSupport = -> [XZ_Plane]
  FullyConstrained = true
  MakeInternals = false
  MapMode = 5
  Placement = pos=(0,0,0) rot=(1,0,0;1.5708rad)
  sketch-geometry (30):
    g0: LineSegment [constr] StartX=-80 StartY=20 StartZ=0 EndX=-80 EndY=-20 EndZ=0
    g1: LineSegment [constr] StartX=-80 StartY=-20 StartZ=0 EndX=-40 EndY=-20 EndZ=0
    g2: LineSegment [constr] StartX=-40 StartY=-20 StartZ=0 EndX=-40 EndY=20 EndZ=0
    g3: LineSegment [constr] StartX=-40 StartY=20 StartZ=0 EndX=-80 EndY=20 EndZ=0
    g4: LineSegment [constr] StartX=40 StartY=20 StartZ=0 EndX=40 EndY=-20 EndZ=0
    g5: LineSegment [constr] StartX=40 StartY=-20 StartZ=0 EndX=80 EndY=-20 EndZ=0
    g6: LineSegment [constr] StartX=80 StartY=-20 StartZ=0 EndX=80 EndY=20 EndZ=0
    g7: LineSegment [constr] StartX=80 StartY=20 StartZ=0 EndX=40 EndY=20 EndZ=0
    g8: LineSegment [constr] StartX=-40 StartY=-20 StartZ=0 EndX=0 EndY=0 EndZ=0
    g9: LineSegment [constr] StartX=0 StartY=0 StartZ=0 EndX=40 EndY=-20 EndZ=0
    g10: LineSegment [constr] StartX=-40 StartY=44.5 StartZ=0 EndX=-40 EndY=-35.5 EndZ=0
    g11: LineSegment [constr] StartX=-40 StartY=-35.5 StartZ=0 EndX=40 EndY=-35.5 EndZ=0
    g12: LineSegment [constr] StartX=40 StartY=-35.5 StartZ=0 EndX=40 EndY=44.5 EndZ=0
    g13: LineSegment [constr] StartX=40 StartY=44.5 StartZ=0 EndX=-40 EndY=44.5 EndZ=0
    g14: LineSegment StartX=40.4 StartY=-20.4 StartZ=0 EndX=72.5 EndY=-20.4 EndZ=0
    g15: LineSegment StartX=72.5 StartY=-20.4 StartZ=0 EndX=72.5 EndY=-30.4 EndZ=0
    g16: LineSegment StartX=-72.5 StartY=-30.4 StartZ=0 EndX=-72.5 EndY=-20.4 EndZ=0
    g17: LineSegment StartX=-72.5 StartY=-20.4 StartZ=0 EndX=-40.4 EndY=-20.4 EndZ=0
    g18: ArcOfCircle [constr] CenterX=-40 CenterY=-35.5 CenterZ=0 NormalX=0 NormalY=0 NormalZ=1 AngleXU=0 Radius=14 StartAngle=3e-16 EndAngle=1.5708
    g19: ArcOfCircle [constr] CenterX=-40 CenterY=44.5 CenterZ=0 NormalX=0 NormalY=0 NormalZ=1 AngleXU=0 Radius=14 StartAngle=4.71239 EndAngle=6.28319
    g20: ArcOfCircle [constr] CenterX=40 CenterY=-35.5 CenterZ=0 NormalX=0 NormalY=0 NormalZ=1 AngleXU=0 Radius=14 StartAngle=1.5708 EndAngle=3.14159
    g21: ArcOfCircle [constr] CenterX=40 CenterY=44.5 CenterZ=0 NormalX=0 NormalY=0 NormalZ=1 AngleXU=0 Radius=14 StartAngle=3.14159 EndAngle=4.71239
    g22: ArcOfCircle CenterX=-40.4 CenterY=-35.9 CenterZ=0 NormalX=0 NormalY=0 NormalZ=1 AngleXU=0 Radius=14 StartAngle=2e-16 EndAngle=1.5708
    g23: ArcOfCircle CenterX=40.4 CenterY=-35.9 CenterZ=0 NormalX=0 NormalY=0 NormalZ=1 AngleXU=0 Radius=14 StartAngle=1.5708 EndAngle=3.14159
    g24: LineSegment StartX=-40.4 StartY=-21.9 StartZ=0 EndX=-40.4 EndY=-20.4 EndZ=0
    g25: LineSegment StartX=-26.4 StartY=-35.9 StartZ=0 EndX=26.4 EndY=-35.9 EndZ=0
    g26: LineSegment StartX=40.4 StartY=-21.9 StartZ=0 EndX=40.4 EndY=-20.4 EndZ=0
    g27: LineSegment StartX=-72.5 StartY=-30.4 StartZ=0 EndX=-26.4 EndY=-40.9 EndZ=0
    g28: LineSegment StartX=-26.4 StartY=-40.9 StartZ=0 EndX=26.4 EndY=-40.9 EndZ=0
    g29: LineSegment StartX=26.4 StartY=-40.9 StartZ=0 EndX=72.5 EndY=-30.4 EndZ=0
  constraints (94):
    c: Coincident(g0,g1)
    c: Coincident(g1,g2)
    c: Coincident(g2,g3)
    c: Coincident(g3,g0)
    c: Vertical(g0)
    c: Vertical(g2)
    c: Horizontal(g1)
    c: Horizontal(g3)
    c: Coincident(g4,g5)
    c: Coincident(g5,g6)
    c: Coincident(g6,g7)
    c: Coincident(g7,g4)
    c: Vertical(g4)
    c: Vertical(g6)
    c: Horizontal(g5)
    c: Horizontal(g7)
    c: Equal(g3,g2)
    c: Equal(g2,g4)
    c: Equal(g4,g7)
    c: DistanceY(g0,g0) = 40
    c: DistanceX(g2,g4) = 80
    c: DistanceY(g2,g4) = 0
    c: Coincident(g8,g1)
    c: Coincident(g8,g-1)
    c: Coincident(g9,g8)
    c: Coincident(g9,g4)
    c: Equal(g9,g8)
    c: Coincident(g10,g11)
    c: Coincident(g11,g12)
    c: Coincident(g12,g13)
    c: Coincident(g13,g10)
    c: Vertical(g10)
    c: Vertical(g12)
    c: Horizontal(g11)
    c: Horizontal(g13)
    c: PointOnObject(g2,g10)
    c: PointOnObject(g4,g12)
    c: Equal(g13,g10)
    c: DistanceY(g2,g10) = 24.5
    c: DistanceY(g2) = 20
    c: Horizontal(g14)
    c: Coincident(g14,g15)
    c: Vertical(g15)
    c: Vertical(g16)
    c: Coincident(g16,g17)
    c: Horizontal(g17)
    c: DistanceY(g17,g1) = 0.4
    c: Equal(g16,g15)
    c: DistanceX(g0,g16) = 7.5
    c: DistanceY(g16,g16) = 10
    c: Coincident(g18,g10)
    c: PointOnObject(g18,g10)
    c: PointOnObject(g18,g11)
    c: Diameter(g18) = 28
    c: Coincident(g19,g10)
    c: PointOnObject(g19,g13)
    c: PointOnObject(g19,g10)
    c: Coincident(g20,g11)
    c: PointOnObject(g20,g11)
    c: PointOnObject(g20,g12)
    c: Coincident(g21,g12)
    c: PointOnObject(g21,g13)
    c: PointOnObject(g21,g12)
    c: Equal(g18,g20)
    c: Equal(g20,g21)
    c: Equal(g21,g19)
    c: DistanceX(g17,g1) = 0.4
    c: Coincident(g24,g22)
    c: Coincident(g24,g17)
    c: Vertical(g24)
    c: DistanceY(g22,g18) = 0.4
    c: Coincident(g25,g22)
    c: Coincident(g25,g23)
    c: Horizontal(g25)
    c: DistanceY(g22,g18) = 0.4
    c: Perpendicular(g22,g24)
    c: Perpendicular(g22,g25)
    c: Perpendicular(g23,g25)
    c: Coincident(g26,g23)
    c: Coincident(g26,g14)
    c: Vertical(g26)
    c: Equal(g17,g14)
    c: Equal(g24,g26)
    c: Coincident(g16,g27)
    c: Coincident(g27,g28)
    c: Horizontal(g28)
    c: Coincident(g28,g29)
    c: Coincident(g29,g15)
    c: DistanceX(g27,g22) = 0
    c: DistanceY(g27,g22) = 5
    c: DistanceX(g28,g23) = 0
    c: Equal(g29,g27)
    c: DistanceX(g4,g14) = 0.4
    c: DistanceY(g14,g4) = 0.4
FEATURE [PartDesign::Pad] Pad
  Direction = (0,-1,2e-16)
  Length = 25
  Length2 = 10
  Placement = pos=(0,0,0) rot=(1,0,0;1.5708rad)
  Profile = -> Sketch
  ReferenceAxis = -> Sketch [N_Axis]
  Refine = true
  Suppressed = false
  Type = 0
FEATURE [Sketcher::SketchObject] Sketch001
  ArcFitTolerance = 1e-06
  AttachmentSupport = -> [Pad]
  FullyConstrained = true
  MakeInternals = false
  MapMode = 5
  Placement = pos=(0,-4.5e-15,-20.4) rot=(0,0,1;3.14159rad)
  sketch-geometry (14):
    g0: LineSegment [constr] StartX=-72.5 StartY=0 StartZ=0 EndX=-47.5 EndY=0 EndZ=0
    g1: LineSegment [constr] StartX=-47.5 StartY=0 StartZ=0 EndX=-47.5 EndY=25 EndZ=0
    g2: LineSegment [constr] StartX=-47.5 StartY=25 StartZ=0 EndX=-72.5 EndY=25 EndZ=0
    g3: LineSegment [constr] StartX=-72.5 StartY=25 StartZ=0 EndX=-72.5 EndY=0 EndZ=0
    g4: LineSegment [constr] StartX=72.5 StartY=0 StartZ=0 EndX=72.5 EndY=25 EndZ=0
    g5: LineSegment [constr] StartX=72.5 StartY=25 StartZ=0 EndX=47.5 EndY=25 EndZ=0
    g6: LineSegment [constr] StartX=47.5 StartY=25 StartZ=0 EndX=47.5 EndY=0 EndZ=0
    g7: LineSegment [constr] StartX=47.5 StartY=0 StartZ=0 EndX=72.5 EndY=0 EndZ=0
    g8: LineSegment [constr] StartX=-72.5 StartY=25 StartZ=0 EndX=-47.5 EndY=0 EndZ=0
    g9: LineSegment [constr] StartX=-72.5 StartY=0 StartZ=0 EndX=-47.5 EndY=25 EndZ=0
    g10: LineSegment [constr] StartX=47.5 StartY=25 StartZ=0 EndX=72.5 EndY=0 EndZ=0
    g11: LineSegment [constr] StartX=47.5 StartY=0 StartZ=0 EndX=72.5 EndY=25 EndZ=0
    g12: Circle CenterX=-60 CenterY=12.5 CenterZ=0 NormalX=0 NormalY=0 NormalZ=1 AngleXU=0 Radius=4.3
    g13: Circle CenterX=60 CenterY=12.5 CenterZ=0 NormalX=0 NormalY=0 NormalZ=1 AngleXU=0 Radius=4.3
  constraints (36):
    c: Coincident(g0,g1)
    c: Coincident(g1,g2)
    c: Coincident(g2,g3)
    c: Coincident(g3,g0)
    c: Horizontal(g0)
    c: Horizontal(g2)
    c: Vertical(g1)
    c: Vertical(g3)
    c: Distance(g1,g3) = 25
    c: Distance(g0,g2) = 25
    c: PointOnObject(g0,g-1)
    c: DistanceX(g0) = -47.5
    c: Coincident(g4,g5)
    c: Coincident(g5,g6)
    c: Coincident(g6,g7)
    c: Coincident(g7,g4)
    c: Vertical(g4)
    c: Vertical(g6)
    c: Horizontal(g5)
    c: Horizontal(g7)
    c: PointOnObject(g4,g-1)
    c: Equal(g6,g5)
    c: Equal(g5,g1)
    c: DistanceX(g6) = 47.5
    c: Coincident(g8,g2)
    c: Coincident(g8,g0)
    c: Coincident(g9,g0)
    c: Coincident(g9,g1)
    c: Coincident(g10,g5)
    c: Coincident(g10,g4)
    c: Coincident(g11,g6)
    c: Coincident(g11,g4)
    c: Diameter(g12) = 8.6
    c: Symmetric(g8,g8,g12)
    c: Symmetric(g11,g11,g13)
    c: Equal(g13,g12)
FEATURE [PartDesign::Pocket] Pocket
  BaseFeature = -> Pad
  Direction = (0,0,-1)
  Length = 5
  Length2 = 5
  Placement = pos=(0,0,0) rot=(1,0,0;1.5708rad)
  Profile = -> Sketch001
  ReferenceAxis = -> Sketch001 [N_Axis]
  Refine = true
  Suppressed = false
  Type = 1
FEATURE [Sketcher::SketchObject] Sketch002
  ArcFitTolerance = 1e-06
  AttachmentOffset = pos=(0,0,-5) rot=(0,0,1;0rad)
  AttachmentSupport = -> [Pocket]
  FullyConstrained = true
  MakeInternals = false
  MapMode = 5
  Placement = pos=(0,-4.5e-15,-25.4) rot=(0,0,1;3.14159rad)
  expr: Constraints[11] = Sketch001.Constraints[11]
  expr: Constraints[23] = Sketch001.Constraints[23]
  expr: Constraints[32] = Sketch001.Constraints[32]
  expr: Constraints[8] = Sketch001.Constraints[8]
  expr: Constraints[9] = Sketch001.Constraints[9]
  sketch-geometry (16):
    g0: LineSegment [constr] StartX=-72.5 StartY=0 StartZ=0 EndX=-47.5 EndY=0 EndZ=0
    g1: LineSegment [constr] StartX=-47.5 StartY=0 StartZ=0 EndX=-47.5 EndY=25 EndZ=0
    g2: LineSegment [constr] StartX=-47.5 StartY=25 StartZ=0 EndX=-72.5 EndY=25 EndZ=0
    g3: LineSegment [constr] StartX=-72.5 StartY=25 StartZ=0 EndX=-72.5 EndY=0 EndZ=0
    g4: LineSegment [constr] StartX=72.5 StartY=0 StartZ=0 EndX=72.5 EndY=25 EndZ=0
    g5: LineSegment [constr] StartX=72.5 StartY=25 StartZ=0 EndX=47.5 EndY=25 EndZ=0
    g6: LineSegment [constr] StartX=47.5 StartY=25 StartZ=0 EndX=47.5 EndY=0 EndZ=0
    g7: LineSegment [constr] StartX=47.5 StartY=0 StartZ=0 EndX=72.5 EndY=0 EndZ=0
    g8: LineSegment [constr] StartX=-72.5 StartY=25 StartZ=0 EndX=-47.5 EndY=0 EndZ=0
    g9: LineSegment [constr] StartX=-72.5 StartY=0 StartZ=0 EndX=-47.5 EndY=25 EndZ=0
    g10: LineSegment [constr] StartX=47.5 StartY=25 StartZ=0 EndX=72.5 EndY=0 EndZ=0
    g11: LineSegment [constr] StartX=47.5 StartY=0 StartZ=0 EndX=72.5 EndY=25 EndZ=0
    g12: Circle [constr] CenterX=-60 CenterY=12.5 CenterZ=0 NormalX=0 NormalY=0 NormalZ=1 AngleXU=0 Radius=4.3
    g13: Circle [constr] CenterX=60 CenterY=12.5 CenterZ=0 NormalX=0 NormalY=0 NormalZ=1 AngleXU=0 Radius=4.3
    g14: Circle CenterX=-60 CenterY=12.5 CenterZ=0 NormalX=0 NormalY=0 NormalZ=1 AngleXU=0 Radius=6.75
    g15: Circle CenterX=60 CenterY=12.5 CenterZ=0 NormalX=0 NormalY=0 NormalZ=1 AngleXU=0 Radius=6.75
  constraints (40):
    c: Coincident(g0,g1)
    c: Coincident(g1,g2)
    c: Coincident(g2,g3)
    c: Coincident(g3,g0)
    c: Horizontal(g0)
    c: Horizontal(g2)
    c: Vertical(g1)
    c: Vertical(g3)
    c: Distance(g1,g3) = 25
    c: Distance(g0,g2) = 25
    c: PointOnObject(g0,g-1)
    c: DistanceX(g0) = -47.5
    c: Coincident(g4,g5)
    c: Coincident(g5,g6)
    c: Coincident(g6,g7)
    c: Coincident(g7,g4)
    c: Vertical(g4)
    c: Vertical(g6)
    c: Horizontal(g5)
    c: Horizontal(g7)
    c: PointOnObject(g4,g-1)
    c: Equal(g6,g5)
    c: Equal(g5,g1)
    c: DistanceX(g6) = 47.5
    c: Coincident(g8,g2)
    c: Coincident(g8,g0)
    c: Coincident(g9,g0)
    c: Coincident(g9,g1)
    c: Coincident(g10,g5)
    c: Coincident(g10,g4)
    c: Coincident(g11,g6)
    c: Coincident(g11,g4)
    c: Diameter(g12) = 8.6
    c: Symmetric(g8,g8,g12)
    c: Symmetric(g11,g11,g13)
    c: Equal(g13,g12)
    c: Coincident(g14,g12)
    c: Coincident(g15,g13)
    c: Equal(g14,g15)
    c: Diameter(g14) = 13.5
FEATURE [PartDesign::Pocket] Pocket001
  BaseFeature = -> Pocket
  Direction = (0,0,-1)
  Length = 5
  Length2 = 5
  Placement = pos=(0,0,0) rot=(1,0,0;1.5708rad)
  Profile = -> Sketch002
  ReferenceAxis = -> Sketch002 [N_Axis]
  Refine = true
  Suppressed = false
  Type = 1
FEATURE [PartDesign::Fillet] Fillet
  Base = -> Pocket001 [Edge25,Edge16,Edge21,Edge12]
  BaseFeature = -> Pocket001
  Placement = pos=(0,0,0) rot=(1,0,0;1.5708rad)
  Radius = 4
  Refine = true
  SupportTransform = false
  Suppressed = false
  UseAllEdges = false
FEATURE [PartDesign::Fillet] Fillet001
  Base = -> Fillet [Edge41,Edge38]
  BaseFeature = -> Fillet
  Placement = pos=(0,0,0) rot=(1,0,0;1.5708rad)
  Radius = 18
  Refine = true
  SupportTransform = false
  Suppressed = false
  UseAllEdges = false
FEATURE [PartDesign::Body] Body  label="surge_motor_mount_bottom"
  AllowCompound = false
  Group = -> [Sketch,Pad,Sketch001,Pocket,Sketch002,Pocket001,Fillet,Fillet001]
  Origin = -> Origin
  Tip = -> Fillet001
COMPONENT P19 — recipe-attached ("surge_motor_mount_side", a linked part whose construction recipe lives in a companion FreeCAD document of the same project; that document's serialized recipe follows).
Construction recipe (the companion document, serialized — sketch geometry with constraints, then the solid features built on it; lengths are millimeters unless a unit is written):

FCSTD DOCUMENT  (FreeCAD 1.0R39109 (Git))
Label: surge_motor_mount_side
License: All rights reserved
LicenseURL: https://en.wikipedia.org/wiki/All_rights_reserved
objects: Sketcher::SketchObject×7, PartDesign::Pocket×6, PartDesign::Fillet×4, PartDesign::Pad×1, PartDesign::Body×1
note: 48 computed .brp shape members not serialized (recipe doc carries the construction recipe); baked Part::Feature solids carry a one-line shape summary decoded from their .brp

FEATURE [Sketcher::SketchObject] Sketch
  ArcFitTolerance = 1e-06
  AttachmentSupport = -> [XZ_Plane]
  FullyConstrained = true
  MakeInternals = false
  MapMode = 5
  Placement = pos=(0,0,0) rot=(1,0,0;1.5708rad)
  sketch-geometry (48):
    g0: LineSegment [constr] StartX=-80 StartY=20 StartZ=0 EndX=-80 EndY=-20 EndZ=0
    g1: LineSegment [constr] StartX=-80 StartY=-20 StartZ=0 EndX=-40 EndY=-20 EndZ=0
    g2: LineSegment [constr] StartX=-40 StartY=-20 StartZ=0 EndX=-40 EndY=20 EndZ=0
    g3: LineSegment [constr] StartX=-40 StartY=20 StartZ=0 EndX=-80 EndY=20 EndZ=0
    g4: LineSegment [constr] StartX=40 StartY=20 StartZ=0 EndX=40 EndY=-20 EndZ=0
    g5: LineSegment [constr] StartX=40 StartY=-20 StartZ=0 EndX=80 EndY=-20 EndZ=0
    g6: LineSegment [constr] StartX=80 StartY=-20 StartZ=0 EndX=80 EndY=20 EndZ=0
    g7: LineSegment [constr] StartX=80 StartY=20 StartZ=0 EndX=40 EndY=20 EndZ=0
    g8: LineSegment [constr] StartX=-40 StartY=-20 StartZ=0 EndX=0 EndY=0 EndZ=0
    g9: LineSegment [constr] StartX=0 StartY=0 StartZ=0 EndX=40 EndY=-20 EndZ=0
    g10: LineSegment [constr] StartX=-40 StartY=44.5 StartZ=0 EndX=-40 EndY=-35.5 EndZ=0
    g11: LineSegment [constr] StartX=-40 StartY=-35.5 StartZ=0 EndX=40 EndY=-35.5 EndZ=0
    g12: LineSegment [constr] StartX=40 StartY=-35.5 StartZ=0 EndX=40 EndY=44.5 EndZ=0
    g13: LineSegment [constr] StartX=40 StartY=44.5 StartZ=0 EndX=-40 EndY=44.5 EndZ=0
    g14: ArcOfCircle [constr] CenterX=-33 CenterY=37.5 CenterZ=0 NormalX=0 NormalY=0 NormalZ=1 AngleXU=0 Radius=7 StartAngle=1.5708 EndAngle=3.14159
    g15: ArcOfCircle [constr] CenterX=33 CenterY=37.5 CenterZ=0 NormalX=0 NormalY=0 NormalZ=1 AngleXU=0 Radius=7 StartAngle=0 EndAngle=1.5708
    g16: ArcOfCircle [constr] CenterX=33 CenterY=-28.5 CenterZ=0 NormalX=0 NormalY=0 NormalZ=1 AngleXU=0 Radius=7 StartAngle=4.71239 EndAngle=6.28319
    g17: ArcOfCircle [constr] CenterX=-33 CenterY=-28.5 CenterZ=0 NormalX=0 NormalY=0 NormalZ=1 AngleXU=0 Radius=7 StartAngle=3.14159 EndAngle=4.71239
    g18: Circle [constr] CenterX=-31.75 CenterY=36.25 CenterZ=0 NormalX=0 NormalY=0 NormalZ=1 AngleXU=0 Radius=3
    g19: Circle [constr] CenterX=31.75 CenterY=36.25 CenterZ=0 NormalX=0 NormalY=0 NormalZ=1 AngleXU=0 Radius=3
    g20: Circle [constr] CenterX=31.75 CenterY=-27.25 CenterZ=0 NormalX=0 NormalY=0 NormalZ=1 AngleXU=0 Radius=3
    g21: Circle [constr] CenterX=-31.75 CenterY=-27.25 CenterZ=0 NormalX=0 NormalY=0 NormalZ=1 AngleXU=0 Radius=3
    g22: LineSegment [constr] StartX=-40 StartY=-35.5 StartZ=0 EndX=-31.75 EndY=-27.25 EndZ=0
    g23: LineSegment [constr] StartX=31.75 StartY=-27.25 StartZ=0 EndX=40 EndY=-35.5 EndZ=0
    g24: LineSegment [constr] StartX=-40 StartY=44.5 StartZ=0 EndX=40 EndY=-35.5 EndZ=0
    g25: LineSegment [constr] StartX=-40 StartY=-35.5 StartZ=0 EndX=40 EndY=44.5 EndZ=0
    g26: Circle [constr] CenterX=-1.1e-15 CenterY=4.5 CenterZ=0 NormalX=0 NormalY=0 NormalZ=1 AngleXU=0 Radius=35
    g27: LineSegment StartX=-72.5 StartY=20.4 StartZ=0 EndX=-72.5 EndY=30.4 EndZ=0
    g28: LineSegment StartX=-72.5 StartY=30.4 StartZ=0 EndX=-40 EndY=44.5 EndZ=0
    g29: LineSegment StartX=40 StartY=44.5 StartZ=0 EndX=72.5 EndY=30.4 EndZ=0
    g30: LineSegment StartX=72.5 StartY=30.4 StartZ=0 EndX=72.5 EndY=20.4 EndZ=0
    g31: LineSegment StartX=72.5 StartY=20.4 StartZ=0 EndX=39.6 EndY=20.4 EndZ=0
    g32: LineSegment StartX=39.6 StartY=20.4 StartZ=0 EndX=39.6 EndY=-20.4 EndZ=0
    g33: LineSegment StartX=39.6 StartY=-20.4 StartZ=0 EndX=72.5 EndY=-20.4 EndZ=0
    g34: LineSegment StartX=72.5 StartY=-20.4 StartZ=0 EndX=72.5 EndY=-30.4 EndZ=0
    g35: LineSegment StartX=72.5 StartY=-30.4 StartZ=0 EndX=40 EndY=-35.5 EndZ=0
    g36: LineSegment StartX=40 StartY=-35.5 StartZ=0 EndX=-40 EndY=-35.5 EndZ=0
    g37: LineSegment StartX=-40 StartY=-35.5 StartZ=0 EndX=-72.5 EndY=-30.4 EndZ=0
    g38: LineSegment StartX=-72.5 StartY=-30.4 StartZ=0 EndX=-72.5 EndY=-20.4 EndZ=0
    g39: LineSegment StartX=-72.5 StartY=-20.4 StartZ=0 EndX=-39.6 EndY=-20.4 EndZ=0
    g40: LineSegment StartX=-39.6 StartY=-20.4 StartZ=0 EndX=-39.6 EndY=20.4 EndZ=0
    g41: LineSegment StartX=-39.6 StartY=20.4 StartZ=0 EndX=-72.5 EndY=20.4 EndZ=0
    g42: Circle [constr] CenterX=-1.1e-15 CenterY=4.5 CenterZ=0 NormalX=0 NormalY=0 NormalZ=1 AngleXU=0 Radius=35.4
    g43: ArcOfCircle CenterX=-1.1e-15 CenterY=4.5 CenterZ=0 NormalX=0 NormalY=0 NormalZ=1 AngleXU=0 Radius=35.4 StartAngle=2.1712 EndAngle=7.25358
    g44: LineSegment StartX=-40 StartY=44.5 StartZ=0 EndX=-20 EndY=44.5 EndZ=0
    g45: LineSegment StartX=-20 StartY=44.5 StartZ=0 EndX=-20 EndY=33.7089 EndZ=0
    g46: LineSegment StartX=40 StartY=44.5 StartZ=0 EndX=20 EndY=44.5 EndZ=0
    g47: LineSegment StartX=20 StartY=44.5 StartZ=0 EndX=20 EndY=33.7089 EndZ=0
  constraints (132):
    c: Coincident(g0,g1)
    c: Coincident(g1,g2)
    c: Coincident(g2,g3)
    c: Coincident(g3,g0)
    c: Vertical(g0)
    c: Vertical(g2)
    c: Horizontal(g1)
    c: Horizontal(g3)
    c: Coincident(g4,g5)
    c: Coincident(g5,g6)
    c: Coincident(g6,g7)
    c: Coincident(g7,g4)
    c: Vertical(g4)
    c: Vertical(g6)
    c: Horizontal(g5)
    c: Horizontal(g7)
    c: Equal(g3,g2)
    c: Equal(g2,g4)
    c: Equal(g4,g7)
    c: DistanceY(g0,g0) = 40
    c: DistanceX(g2,g4) = 80
    c: DistanceY(g2,g4) = 0
    c: Coincident(g8,g1)
    c: Coincident(g8,g-1)
    c: Coincident(g9,g8)
    c: Coincident(g9,g4)
    c: Equal(g9,g8)
    c: Coincident(g10,g11)
    c: Coincident(g11,g12)
    c: Coincident(g12,g13)
    c: Coincident(g13,g10)
    c: Vertical(g10)
    c: Vertical(g12)
    c: Horizontal(g11)
    c: Horizontal(g13)
    c: PointOnObject(g2,g10)
    c: PointOnObject(g4,g12)
    c: Equal(g13,g10)
    c: Equal(g16,g17)
    c: Equal(g17,g14)
    c: Equal(g14,g15)
    c: Diameter(g14) = 14
    c: Tangent(g14,g13) = -1.5708
    c: Tangent(g14,g10) = -1.5708
    c: Tangent(g15,g12) = -1.5708
    c: Tangent(g15,g13) = -1.5708
    c: Tangent(g17,g10) = -1.5708
    c: Tangent(g17,g11) = -1.5708
    c: Tangent(g16,g11) = -1.5708
    c: Tangent(g16,g12) = -1.5708
    c: Equal(g21,g20)
    c: Equal(g20,g19)
    c: Equal(g19,g18)
    c: Diameter(g18) = 6
    c: DistanceX(g18,g19) = 63.5
    c: DistanceY(g21,g18) = 63.5
    c: DistanceY(g21,g20) = 0
    c: DistanceY(g19,g18) = 0
    c: DistanceX(g18,g21) = 0
    c: DistanceX(g20,g19) = 0
    c: Coincident(g22,g10)
    c: Coincident(g22,g21)
    c: PointOnObject(g17,g22)
    c: Coincident(g23,g20)
    c: Coincident(g23,g11)
    c: PointOnObject(g16,g23)
    c: DistanceY(g2,g10) = 24.5
    c: DistanceY(g2) = 20
    c: Coincident(g24,g10)
    c: Coincident(g24,g11)
    c: Coincident(g25,g10)
    c: Coincident(g25,g12)
    c: Symmetric(g25,g25,g26)
    c: Diameter(g26) = 70
    c: Vertical(g27)
    c: Coincident(g27,g28)
    c: Coincident(g28,g10)
    c: Coincident(g29,g30)
    c: Vertical(g30)
    c: Coincident(g30,g31)
    c: Horizontal(g31)
    c: Coincident(g31,g32)
    c: Vertical(g32)
    c: Coincident(g32,g33)
    c: Horizontal(g33)
    c: Coincident(g33,g34)
    c: Vertical(g34)
    c: Coincident(g34,g35)
    c: Coincident(g35,g11)
    c: Coincident(g35,g36)
    c: Coincident(g36,g10)
    c: Coincident(g10,g37)
    c: Coincident(g37,g38)
    c: Vertical(g38)
    c: Coincident(g38,g39)
    c: Horizontal(g39)
    c: Coincident(g39,g40)
    c: Vertical(g40)
    c: Coincident(g40,g41)
    c: Coincident(g41,g27)
    c: Horizontal(g41)
    c: DistanceX(g0,g27) = 7.5
    c: DistanceY(g0,g27) = 0.4
    c: DistanceX(g2,g40) = 0.4
    c: DistanceY(g39,g1) = 0.4
    c: Equal(g39,g41)
    c: Equal(g41,g33)
    c: Equal(g33,g31)
    c: DistanceY(g27,g27) = 10
    c: Equal(g27,g38)
    c: Equal(g38,g34)
    c: Equal(g34,g30)
    c: Equal(g32,g40)
    c: Equal(g29,g28)
    c: Equal(g35,g37)
    c: Coincident(g42,g26)
    c: Diameter(g42) = 70.8
    c: Coincident(g43,g26)
    c: PointOnObject(g43,g42)
    c: Coincident(g10,g44)
    c: PointOnObject(g44,g13)
    c: Coincident(g44,g45)
    c: Coincident(g45,g43)
    c: Vertical(g45)
    c: Coincident(g29,g46)
    c: Horizontal(g46)
    c: Coincident(g46,g47)
    c: Coincident(g47,g43)
    c: Vertical(g47)
    c: Equal(g44,g46)
    c: DistanceX(g44,g46) = 40
    c: Coincident(g29,g12)
FEATURE [PartDesign::Pad] Pad
  Direction = (0,-1,2e-16)
  Length = 25
  Length2 = 10
  Placement = pos=(0,0,0) rot=(1,0,0;1.5708rad)
  Profile = -> Sketch
  ReferenceAxis = -> Sketch [N_Axis]
  Refine = true
  Suppressed = false
  Type = 0
FEATURE [Sketcher::SketchObject] Sketch001
  ArcFitTolerance = 1e-06
  AttachmentSupport = -> [Pad]
  FullyConstrained = true
  MakeInternals = false
  MapMode = 5
  Placement = pos=(0,-9e-15,-20.4) rot=(0,0,1;3.14159rad)
  sketch-geometry (14):
    g0: LineSegment [constr] StartX=-72.5 StartY=0 StartZ=0 EndX=-47.5 EndY=0 EndZ=0
    g1: LineSegment [constr] StartX=-47.5 StartY=0 StartZ=0 EndX=-47.5 EndY=25 EndZ=0
    g2: LineSegment [constr] StartX=-47.5 StartY=25 StartZ=0 EndX=-72.5 EndY=25 EndZ=0
    g3: LineSegment [constr] StartX=-72.5 StartY=25 StartZ=0 EndX=-72.5 EndY=0 EndZ=0
    g4: LineSegment [constr] StartX=72.5 StartY=0 StartZ=0 EndX=72.5 EndY=25 EndZ=0
    g5: LineSegment [constr] StartX=72.5 StartY=25 StartZ=0 EndX=47.5 EndY=25 EndZ=0
    g6: LineSegment [constr] StartX=47.5 StartY=25 StartZ=0 EndX=47.5 EndY=0 EndZ=0
    g7: LineSegment [constr] StartX=47.5 StartY=0 StartZ=0 EndX=72.5 EndY=0 EndZ=0
    g8: LineSegment [constr] StartX=-72.5 StartY=25 StartZ=0 EndX=-47.5 EndY=0 EndZ=0
    g9: LineSegment [constr] StartX=-72.5 StartY=0 StartZ=0 EndX=-47.5 EndY=25 EndZ=0
    g10: LineSegment [constr] StartX=47.5 StartY=25 StartZ=0 EndX=72.5 EndY=0 EndZ=0
    g11: LineSegment [constr] StartX=47.5 StartY=0 StartZ=0 EndX=72.5 EndY=25 EndZ=0
    g12: Circle CenterX=-60 CenterY=12.5 CenterZ=0 NormalX=0 NormalY=0 NormalZ=1 AngleXU=0 Radius=4.3
    g13: Circle CenterX=60 CenterY=12.5 CenterZ=0 NormalX=0 NormalY=0 NormalZ=1 AngleXU=0 Radius=4.3
  constraints (36):
    c: Coincident(g0,g1)
    c: Coincident(g1,g2)
    c: Coincident(g2,g3)
    c: Coincident(g3,g0)
    c: Horizontal(g0)
    c: Horizontal(g2)
    c: Vertical(g1)
    c: Vertical(g3)
    c: Distance(g1,g3) = 25
    c: Distance(g0,g2) = 25
    c: PointOnObject(g0,g-1)
    c: DistanceX(g0) = -47.5
    c: Coincident(g4,g5)
    c: Coincident(g5,g6)
    c: Coincident(g6,g7)
    c: Coincident(g7,g4)
    c: Vertical(g4)
    c: Vertical(g6)
    c: Horizontal(g5)
    c: Horizontal(g7)
    c: PointOnObject(g4,g-1)
    c: Equal(g6,g5)
    c: Equal(g5,g1)
    c: DistanceX(g6) = 47.5
    c: Coincident(g8,g2)
    c: Coincident(g8,g0)
    c: Coincident(g9,g0)
    c: Coincident(g9,g1)
    c: Coincident(g10,g5)
    c: Coincident(g10,g4)
    c: Coincident(g11,g6)
    c: Coincident(g11,g4)
    c: Diameter(g12) = 8.6
    c: Symmetric(g8,g8,g12)
    c: Symmetric(g11,g11,g13)
    c: Equal(g13,g12)
FEATURE [PartDesign::Pocket] Pocket
  BaseFeature = -> Pad
  Direction = (0,0,-1)
  Length = 100
  Length2 = 100
  Placement = pos=(0,0,0) rot=(1,0,0;1.5708rad)
  Profile = -> Sketch001
  ReferenceAxis = -> Sketch001 [N_Axis]
  Refine = true
  Suppressed = false
  Type = 4
FEATURE [Sketcher::SketchObject] Sketch002
  ArcFitTolerance = 1e-06
  AttachmentOffset = pos=(0,0,-5) rot=(0,0,1;0rad)
  AttachmentSupport = -> [Pocket]
  FullyConstrained = true
  MakeInternals = false
  MapMode = 5
  Placement = pos=(0,-9e-15,-25.4) rot=(0,0,1;3.14159rad)
  expr: Constraints[11] = Sketch001.Constraints[11]
  expr: Constraints[23] = Sketch001.Constraints[23]
  expr: Constraints[32] = Sketch001.Constraints[32]
  expr: Constraints[8] = Sketch001.Constraints[8]
  expr: Constraints[9] = Sketch001.Constraints[9]
  sketch-geometry (16):
    g0: LineSegment [constr] StartX=-72.5 StartY=0 StartZ=0 EndX=-47.5 EndY=0 EndZ=0
    g1: LineSegment [constr] StartX=-47.5 StartY=0 StartZ=0 EndX=-47.5 EndY=25 EndZ=0
    g2: LineSegment [constr] StartX=-47.5 StartY=25 StartZ=0 EndX=-72.5 EndY=25 EndZ=0
    g3: LineSegment [constr] StartX=-72.5 StartY=25 StartZ=0 EndX=-72.5 EndY=0 EndZ=0
    g4: LineSegment [constr] StartX=72.5 StartY=0 StartZ=0 EndX=72.5 EndY=25 EndZ=0
    g5: LineSegment [constr] StartX=72.5 StartY=25 StartZ=0 EndX=47.5 EndY=25 EndZ=0
    g6: LineSegment [constr] StartX=47.5 StartY=25 StartZ=0 EndX=47.5 EndY=0 EndZ=0
    g7: LineSegment [constr] StartX=47.5 StartY=0 StartZ=0 EndX=72.5 EndY=0 EndZ=0
    g8: LineSegment [constr] StartX=-72.5 StartY=25 StartZ=0 EndX=-47.5 EndY=0 EndZ=0
    g9: LineSegment [constr] StartX=-72.5 StartY=0 StartZ=0 EndX=-47.5 EndY=25 EndZ=0
    g10: LineSegment [constr] StartX=47.5 StartY=25 StartZ=0 EndX=72.5 EndY=0 EndZ=0
    g11: LineSegment [constr] StartX=47.5 StartY=0 StartZ=0 EndX=72.5 EndY=25 EndZ=0
    g12: Circle [constr] CenterX=-60 CenterY=12.5 CenterZ=0 NormalX=0 NormalY=0 NormalZ=1 AngleXU=0 Radius=4.3
    g13: Circle [constr] CenterX=60 CenterY=12.5 CenterZ=0 NormalX=0 NormalY=0 NormalZ=1 AngleXU=0 Radius=4.3
    g14: Circle CenterX=-60 CenterY=12.5 CenterZ=0 NormalX=0 NormalY=0 NormalZ=1 AngleXU=0 Radius=6.75
    g15: Circle CenterX=60 CenterY=12.5 CenterZ=0 NormalX=0 NormalY=0 NormalZ=1 AngleXU=0 Radius=6.75
  constraints (40):
    c: Coincident(g0,g1)
    c: Coincident(g1,g2)
    c: Coincident(g2,g3)
    c: Coincident(g3,g0)
    c: Horizontal(g0)
    c: Horizontal(g2)
    c: Vertical(g1)
    c: Vertical(g3)
    c: Distance(g1,g3) = 25
    c: Distance(g0,g2) = 25
    c: PointOnObject(g0,g-1)
    c: DistanceX(g0) = -47.5
    c: Coincident(g4,g5)
    c: Coincident(g5,g6)
    c: Coincident(g6,g7)
    c: Coincident(g7,g4)
    c: Vertical(g4)
    c: Vertical(g6)
    c: Horizontal(g5)
    c: Horizontal(g7)
    c: PointOnObject(g4,g-1)
    c: Equal(g6,g5)
    c: Equal(g5,g1)
    c: DistanceX(g6) = 47.5
    c: Coincident(g8,g2)
    c: Coincident(g8,g0)
    c: Coincident(g9,g0)
    c: Coincident(g9,g1)
    c: Coincident(g10,g5)
    c: Coincident(g10,g4)
    c: Coincident(g11,g6)
    c: Coincident(g11,g4)
    c: Diameter(g12) = 8.6
    c: Symmetric(g8,g8,g12)
    c: Symmetric(g11,g11,g13)
    c: Equal(g13,g12)
    c: Diameter(g14) = 13.5
    c: Coincident(g14,g12)
    c: Coincident(g15,g13)
    c: Equal(g15,g14)
FEATURE [PartDesign::Pocket] Pocket001
  BaseFeature = -> Pocket
  Direction = (0,0,-1)
  Length = 5
  Length2 = 5
  Placement = pos=(0,0,0) rot=(1,0,0;1.5708rad)
  Profile = -> Sketch002
  ReferenceAxis = -> Sketch002 [N_Axis]
  Refine = true
  Suppressed = false
  Type = 1
FEATURE [Sketcher::SketchObject] Sketch003
  ArcFitTolerance = 1e-06
  AttachmentOffset = pos=(0,0,45.8) rot=(0,0,1;0rad)
  AttachmentSupport = -> [Pocket001]
  FullyConstrained = true
  MakeInternals = false
  MapMode = 5
  Placement = pos=(0,-9e-15,25.4) rot=(0,0,1;3.14159rad)
  expr: Constraints[11] = Sketch002.Constraints[11]
  expr: Constraints[23] = Sketch002.Constraints[23]
  expr: Constraints[32] = Sketch002.Constraints[32]
  expr: Constraints[36] = Sketch002.Constraints[36]
  expr: Constraints[8] = Sketch002.Constraints[8]
  expr: Constraints[9] = Sketch002.Constraints[9]
  sketch-geometry (16):
    g0: LineSegment [constr] StartX=-72.5 StartY=0 StartZ=0 EndX=-47.5 EndY=0 EndZ=0
    g1: LineSegment [constr] StartX=-47.5 StartY=0 StartZ=0 EndX=-47.5 EndY=25 EndZ=0
    g2: LineSegment [constr] StartX=-47.5 StartY=25 StartZ=0 EndX=-72.5 EndY=25 EndZ=0
    g3: LineSegment [constr] StartX=-72.5 StartY=25 StartZ=0 EndX=-72.5 EndY=0 EndZ=0
    g4: LineSegment [constr] StartX=72.5 StartY=0 StartZ=0 EndX=72.5 EndY=25 EndZ=0
    g5: LineSegment [constr] StartX=72.5 StartY=25 StartZ=0 EndX=47.5 EndY=25 EndZ=0
    g6: LineSegment [constr] StartX=47.5 StartY=25 StartZ=0 EndX=47.5 EndY=0 EndZ=0
    g7: LineSegment [constr] StartX=47.5 StartY=0 StartZ=0 EndX=72.5 EndY=0 EndZ=0
    g8: LineSegment [constr] StartX=-72.5 StartY=25 StartZ=0 EndX=-47.5 EndY=0 EndZ=0
    g9: LineSegment [constr] StartX=-72.5 StartY=0 StartZ=0 EndX=-47.5 EndY=25 EndZ=0
    g10: LineSegment [constr] StartX=47.5 StartY=25 StartZ=0 EndX=72.5 EndY=0 EndZ=0
    g11: LineSegment [constr] StartX=47.5 StartY=0 StartZ=0 EndX=72.5 EndY=25 EndZ=0
    g12: Circle [constr] CenterX=-60 CenterY=12.5 CenterZ=0 NormalX=0 NormalY=0 NormalZ=1 AngleXU=0 Radius=4.3
    g13: Circle [constr] CenterX=60 CenterY=12.5 CenterZ=0 NormalX=0 NormalY=0 NormalZ=1 AngleXU=0 Radius=4.3
    g14: Circle CenterX=-60 CenterY=12.5 CenterZ=0 NormalX=0 NormalY=0 NormalZ=1 AngleXU=0 Radius=6.75
    g15: Circle CenterX=60 CenterY=12.5 CenterZ=0 NormalX=0 NormalY=0 NormalZ=1 AngleXU=0 Radius=6.75
  constraints (40):
    c: Coincident(g0,g1)
    c: Coincident(g1,g2)
    c: Coincident(g2,g3)
    c: Coincident(g3,g0)
    c: Horizontal(g0)
    c: Horizontal(g2)
    c: Vertical(g1)
    c: Vertical(g3)
    c: Distance(g1,g3) = 25
    c: Distance(g0,g2) = 25
    c: PointOnObject(g0,g-1)
    c: DistanceX(g0) = -47.5
    c: Coincident(g4,g5)
    c: Coincident(g5,g6)
    c: Coincident(g6,g7)
    c: Coincident(g7,g4)
    c: Vertical(g4)
    c: Vertical(g6)
    c: Horizontal(g5)
    c: Horizontal(g7)
    c: PointOnObject(g4,g-1)
    c: Equal(g6,g5)
    c: Equal(g5,g1)
    c: DistanceX(g6) = 47.5
    c: Coincident(g8,g2)
    c: Coincident(g8,g0)
    c: Coincident(g9,g0)
    c: Coincident(g9,g1)
    c: Coincident(g10,g5)
    c: Coincident(g10,g4)
    c: Coincident(g11,g6)
    c: Coincident(g11,g4)
    c: Diameter(g12) = 8.6
    c: Symmetric(g8,g8,g12)
    c: Symmetric(g11,g11,g13)
    c: Equal(g13,g12)
    c: Diameter(g14) = 13.5
    c: Coincident(g14,g12)
    c: Coincident(g15,g13)
    c: Equal(g15,g14)
FEATURE [PartDesign::Pocket] Pocket002
  BaseFeature = -> Pocket001
  Direction = (0,0,-1)
  Length = 5
  Length2 = 5
  Placement = pos=(0,0,0) rot=(1,0,0;1.5708rad)
  Profile = -> Sketch003
  ReferenceAxis = -> Sketch003 [N_Axis]
  Refine = true
  Reversed = true
  Suppressed = false
  Type = 1
FEATURE [Sketcher::SketchObject] Sketch004
  ArcFitTolerance = 1e-06
  AttachmentSupport = -> [Pocket002]
  FullyConstrained = true
  MakeInternals = false
  MapMode = 5
  Placement = pos=(0,-25,0) rot=(1,0,0;1.5708rad)
  expr: Constraints[104] = Sketch.Constraints[101]
  expr: Constraints[105] = Sketch.Constraints[102]
  expr: Constraints[106] = Sketch.Constraints[103]
  expr: Constraints[107] = Sketch.Constraints[104]
  expr: Constraints[111] = Sketch.Constraints[108]
  expr: Constraints[119] = Sketch.Constraints[116]
  expr: Constraints[19] = Sketch.Constraints[19]
  expr: Constraints[20] = Sketch.Constraints[20]
  expr: Constraints[21] = Sketch.Constraints[21]
  expr: Constraints[41] = Sketch.Constraints[41]
  expr: Constraints[53] = Sketch.Constraints[53]
  expr: Constraints[54] = Sketch.Constraints[54]
  expr: Constraints[55] = Sketch.Constraints[55]
  expr: Constraints[56] = Sketch.Constraints[56]
  expr: Constraints[57] = Sketch.Constraints[57]
  expr: Constraints[58] = Sketch.Constraints[58]
  expr: Constraints[59] = Sketch.Constraints[59]
  expr: Constraints[66] = Sketch.Constraints[66]
  expr: Constraints[67] = Sketch.Constraints[67]
  expr: Constraints[73] = Sketch.Constraints[73]
  sketch-geometry (48):
    g0: LineSegment [constr] StartX=-80 StartY=20 StartZ=0 EndX=-80 EndY=-20 EndZ=0
    g1: LineSegment [constr] StartX=-80 StartY=-20 StartZ=0 EndX=-40 EndY=-20 EndZ=0
    g2: LineSegment [constr] StartX=-40 StartY=-20 StartZ=0 EndX=-40 EndY=20 EndZ=0
    g3: LineSegment [constr] StartX=-40 StartY=20 StartZ=0 EndX=-80 EndY=20 EndZ=0
    g4: LineSegment [constr] StartX=40 StartY=20 StartZ=0 EndX=40 EndY=-20 EndZ=0
    g5: LineSegment [constr] StartX=40 StartY=-20 StartZ=0 EndX=80 EndY=-20 EndZ=0
    g6: LineSegment [constr] StartX=80 StartY=-20 StartZ=0 EndX=80 EndY=20 EndZ=0
    g7: LineSegment [constr] StartX=80 StartY=20 StartZ=0 EndX=40 EndY=20 EndZ=0
    g8: LineSegment [constr] StartX=-40 StartY=-20 StartZ=0 EndX=0 EndY=0 EndZ=0
    g9: LineSegment [constr] StartX=0 StartY=0 StartZ=0 EndX=40 EndY=-20 EndZ=0
    g10: LineSegment [constr] StartX=-40 StartY=44.5 StartZ=0 EndX=-40 EndY=-35.5 EndZ=0
    g11: LineSegment [constr] StartX=-40 StartY=-35.5 StartZ=0 EndX=40 EndY=-35.5 EndZ=0
    g12: LineSegment [constr] StartX=40 StartY=-35.5 StartZ=0 EndX=40 EndY=44.5 EndZ=0
    g13: LineSegment [constr] StartX=40 StartY=44.5 StartZ=0 EndX=-40 EndY=44.5 EndZ=0
    g14: ArcOfCircle [constr] CenterX=-33 CenterY=37.5 CenterZ=0 NormalX=0 NormalY=0 NormalZ=1 AngleXU=0 Radius=7 StartAngle=1.5708 EndAngle=3.14159
    g15: ArcOfCircle [constr] CenterX=33 CenterY=37.5 CenterZ=0 NormalX=0 NormalY=0 NormalZ=1 AngleXU=0 Radius=7 StartAngle=4e-16 EndAngle=1.5708
    g16: ArcOfCircle [constr] CenterX=33 CenterY=-28.5 CenterZ=0 NormalX=0 NormalY=0 NormalZ=1 AngleXU=0 Radius=7 StartAngle=4.71239 EndAngle=6.28319
    g17: ArcOfCircle [constr] CenterX=-33 CenterY=-28.5 CenterZ=0 NormalX=0 NormalY=0 NormalZ=1 AngleXU=0 Radius=7 StartAngle=3.14159 EndAngle=4.71239
    g18: Circle [constr] CenterX=-31.75 CenterY=36.25 CenterZ=0 NormalX=0 NormalY=0 NormalZ=1 AngleXU=0 Radius=3
    g19: Circle [constr] CenterX=31.75 CenterY=36.25 CenterZ=0 NormalX=0 NormalY=0 NormalZ=1 AngleXU=0 Radius=3
    g20: Circle [constr] CenterX=31.75 CenterY=-27.25 CenterZ=0 NormalX=0 NormalY=0 NormalZ=1 AngleXU=0 Radius=3
    g21: Circle [constr] CenterX=-31.75 CenterY=-27.25 CenterZ=0 NormalX=0 NormalY=0 NormalZ=1 AngleXU=0 Radius=3
    g22: LineSegment [constr] StartX=-40 StartY=-35.5 StartZ=0 EndX=-31.75 EndY=-27.25 EndZ=0
    g23: LineSegment [constr] StartX=31.75 StartY=-27.25 StartZ=0 EndX=40 EndY=-35.5 EndZ=0
    g24: LineSegment [constr] StartX=-40 StartY=44.5 StartZ=0 EndX=40 EndY=-35.5 EndZ=0
    g25: LineSegment [constr] StartX=-40 StartY=-35.5 StartZ=0 EndX=40 EndY=44.5 EndZ=0
    g26: Circle [constr] CenterX=8e-16 CenterY=4.5 CenterZ=0 NormalX=0 NormalY=0 NormalZ=1 AngleXU=0 Radius=35
    g27: LineSegment [constr] StartX=-72.5 StartY=20.4 StartZ=0 EndX=-72.5 EndY=30.4 EndZ=0
    g28: LineSegment [constr] StartX=-72.5 StartY=30.4 StartZ=0 EndX=-40 EndY=44.5 EndZ=0
    g29: LineSegment [constr] StartX=-40 StartY=44.5 StartZ=0 EndX=40 EndY=44.5 EndZ=0
    g30: LineSegment [constr] StartX=40 StartY=44.5 StartZ=0 EndX=72.5 EndY=30.4 EndZ=0
    g31: LineSegment [constr] StartX=72.5 StartY=30.4 StartZ=0 EndX=72.5 EndY=20.4 EndZ=0
    g32: LineSegment [constr] StartX=72.5 StartY=20.4 StartZ=0 EndX=39.6 EndY=20.4 EndZ=0
    g33: LineSegment [constr] StartX=39.6 StartY=20.4 StartZ=0 EndX=39.6 EndY=-20.4 EndZ=0
    g34: LineSegment [constr] StartX=39.6 StartY=-20.4 StartZ=0 EndX=72.5 EndY=-20.4 EndZ=0
    g35: LineSegment [constr] StartX=72.5 StartY=-20.4 StartZ=0 EndX=72.5 EndY=-30.4 EndZ=0
    g36: LineSegment [constr] StartX=72.5 StartY=-30.4 StartZ=0 EndX=40 EndY=-35.5 EndZ=0
    g37: LineSegment [constr] StartX=40 StartY=-35.5 StartZ=0 EndX=-40 EndY=-35.5 EndZ=0
    g38: LineSegment [constr] StartX=-40 StartY=-35.5 StartZ=0 EndX=-72.5 EndY=-30.4 EndZ=0
    g39: LineSegment [constr] StartX=-72.5 StartY=-30.4 StartZ=0 EndX=-72.5 EndY=-20.4 EndZ=0
    g40: LineSegment [constr] StartX=-72.5 StartY=-20.4 StartZ=0 EndX=-39.6 EndY=-20.4 EndZ=0
    g41: LineSegment [constr] StartX=-39.6 StartY=-20.4 StartZ=0 EndX=-39.6 EndY=20.4 EndZ=0
    g42: LineSegment [constr] StartX=-39.6 StartY=20.4 StartZ=0 EndX=-72.5 EndY=20.4 EndZ=0
    g43: Circle [constr] CenterX=8e-16 CenterY=4.5 CenterZ=0 NormalX=0 NormalY=0 NormalZ=1 AngleXU=0 Radius=35.4
    g44: Circle CenterX=-31.75 CenterY=36.25 CenterZ=0 NormalX=0 NormalY=0 NormalZ=1 AngleXU=0 Radius=3.3
    g45: Circle CenterX=31.75 CenterY=36.25 CenterZ=0 NormalX=0 NormalY=0 NormalZ=1 AngleXU=0 Radius=3.3
    g46: Circle CenterX=31.75 CenterY=-27.25 CenterZ=0 NormalX=0 NormalY=0 NormalZ=1 AngleXU=0 Radius=3.3
    g47: Circle CenterX=-31.75 CenterY=-27.25 CenterZ=0 NormalX=0 NormalY=0 NormalZ=1 AngleXU=0 Radius=3.3
  constraints (128):
    c: Coincident(g0,g1)
    c: Coincident(g1,g2)
    c: Coincident(g2,g3)
    c: Coincident(g3,g0)
    c: Vertical(g0)
    c: Vertical(g2)
    c: Horizontal(g1)
    c: Horizontal(g3)
    c: Coincident(g4,g5)
    c: Coincident(g5,g6)
    c: Coincident(g6,g7)
    c: Coincident(g7,g4)
    c: Vertical(g4)
    c: Vertical(g6)
    c: Horizontal(g5)
    c: Horizontal(g7)
    c: Equal(g3,g2)
    c: Equal(g2,g4)
    c: Equal(g4,g7)
    c: DistanceY(g0,g0) = 40
    c: DistanceX(g2,g4) = 80
    c: DistanceY(g2,g4) = 0
    c: Coincident(g8,g1)
    c: Coincident(g8,g-1)
    c: Coincident(g9,g8)
    c: Coincident(g9,g4)
    c: Equal(g9,g8)
    c: Coincident(g10,g11)
    c: Coincident(g11,g12)
    c: Coincident(g12,g13)
    c: Coincident(g13,g10)
    c: Vertical(g10)
    c: Vertical(g12)
    c: Horizontal(g11)
    c: Horizontal(g13)
    c: PointOnObject(g2,g10)
    c: PointOnObject(g4,g12)
    c: Equal(g13,g10)
    c: Equal(g16,g17)
    c: Equal(g17,g14)
    c: Equal(g14,g15)
    c: Diameter(g14) = 14
    c: Tangent(g14,g13) = -1.5708
    c: Tangent(g14,g10) = -1.5708
    c: Tangent(g15,g12) = -1.5708
    c: Tangent(g15,g13) = -1.5708
    c: Tangent(g17,g10) = -1.5708
    c: Tangent(g17,g11) = -1.5708
    c: Tangent(g16,g11) = -1.5708
    c: Tangent(g16,g12) = -1.5708
    c: Equal(g21,g20)
    c: Equal(g20,g19)
    c: Equal(g19,g18)
    c: Diameter(g18) = 6
    c: DistanceX(g18,g19) = 63.5
    c: DistanceY(g21,g18) = 63.5
    c: DistanceY(g21,g20) = 0
    c: DistanceY(g19,g18) = 0
    c: DistanceX(g18,g21) = 0
    c: DistanceX(g20,g19) = 0
    c: Coincident(g22,g10)
    c: Coincident(g22,g21)
    c: PointOnObject(g17,g22)
    c: Coincident(g23,g20)
    c: Coincident(g23,g11)
    c: PointOnObject(g16,g23)
    c: DistanceY(g2,g10) = 24.5
    c: DistanceY(g2) = 20
    c: Coincident(g24,g10)
    c: Coincident(g24,g11)
    c: Coincident(g25,g10)
    c: Coincident(g25,g12)
    c: Symmetric(g25,g25,g26)
    c: Diameter(g26) = 70
    c: Vertical(g27)
    c: Coincident(g27,g28)
    c: Coincident(g28,g10)
    c: Coincident(g28,g29)
    c: Coincident(g29,g12)
    c: Coincident(g29,g30)
    c: Coincident(g30,g31)
    c: Vertical(g31)
    c: Coincident(g31,g32)
    c: Horizontal(g32)
    c: Coincident(g32,g33)
    c: Vertical(g33)
    c: Coincident(g33,g34)
    c: Horizontal(g34)
    c: Coincident(g34,g35)
    c: Vertical(g35)
    c: Coincident(g35,g36)
    c: Coincident(g36,g11)
    c: Coincident(g36,g37)
    c: Coincident(g37,g10)
    c: Coincident(g10,g38)
    c: Coincident(g38,g39)
    c: Vertical(g39)
    c: Coincident(g39,g40)
    c: Horizontal(g40)
    c: Coincident(g40,g41)
    c: Vertical(g41)
    c: Coincident(g41,g42)
    c: Coincident(g42,g27)
    c: Horizontal(g42)
    c: DistanceX(g0,g27) = 7.5
    c: DistanceY(g0,g27) = 0.4
    c: DistanceX(g2,g41) = 0.4
    c: DistanceY(g40,g1) = 0.4
    c: Equal(g40,g42)
    c: Equal(g42,g34)
    c: Equal(g34,g32)
    c: DistanceY(g27,g27) = 10
    c: Equal(g27,g39)
    c: Equal(g39,g35)
    c: Equal(g35,g31)
    c: Equal(g33,g41)
    c: Equal(g30,g28)
    c: Equal(g36,g38)
    c: Coincident(g43,g26)
    c: Diameter(g43) = 70.8
    c: Coincident(g44,g18)
    c: Diameter(g44) = 6.6
    c: Coincident(g45,g19)
    c: Coincident(g46,g20)
    c: Coincident(g47,g21)
    c: Equal(g47,g46)
    c: Equal(g46,g45)
    c: Equal(g45,g44)
FEATURE [PartDesign::Pocket] Pocket003
  BaseFeature = -> Pocket002
  Direction = (0,1,-2e-16)
  Length = 5
  Length2 = 5
  Placement = pos=(0,0,0) rot=(1,0,0;1.5708rad)
  Profile = -> Sketch004
  ReferenceAxis = -> Sketch004 [N_Axis]
  Refine = true
  Suppressed = false
  Type = 1
FEATURE [Sketcher::SketchObject] Sketch005
  ArcFitTolerance = 1e-06
  AttachmentSupport = -> [Pocket003]
  FullyConstrained = true
  MakeInternals = false
  MapMode = 5
  Placement = pos=(0,-25,0) rot=(1,0,0;1.5708rad)
  expr: Constraints[104] = Sketch.Constraints[101]
  expr: Constraints[105] = Sketch.Constraints[102]
  expr: Constraints[106] = Sketch.Constraints[103]
  expr: Constraints[107] = Sketch.Constraints[104]
  expr: Constraints[111] = Sketch.Constraints[108]
  expr: Constraints[119] = Sketch.Constraints[116]
  expr: Constraints[19] = Sketch.Constraints[19]
  expr: Constraints[20] = Sketch.Constraints[20]
  expr: Constraints[21] = Sketch.Constraints[21]
  expr: Constraints[41] = Sketch.Constraints[41]
  expr: Constraints[53] = Sketch.Constraints[53]
  expr: Constraints[54] = Sketch.Constraints[54]
  expr: Constraints[55] = Sketch.Constraints[55]
  expr: Constraints[56] = Sketch.Constraints[56]
  expr: Constraints[57] = Sketch.Constraints[57]
  expr: Constraints[58] = Sketch.Constraints[58]
  expr: Constraints[59] = Sketch.Constraints[59]
  expr: Constraints[66] = Sketch.Constraints[66]
  expr: Constraints[67] = Sketch.Constraints[67]
  expr: Constraints[73] = Sketch.Constraints[73]
  sketch-geometry (72):
    g0: LineSegment [constr] StartX=-80 StartY=20 StartZ=0 EndX=-80 EndY=-20 EndZ=0
    g1: LineSegment [constr] StartX=-80 StartY=-20 StartZ=0 EndX=-40 EndY=-20 EndZ=0
    g2: LineSegment [constr] StartX=-40 StartY=-20 StartZ=0 EndX=-40 EndY=20 EndZ=0
    g3: LineSegment [constr] StartX=-40 StartY=20 StartZ=0 EndX=-80 EndY=20 EndZ=0
    g4: LineSegment [constr] StartX=40 StartY=20 StartZ=0 EndX=40 EndY=-20 EndZ=0
    g5: LineSegment [constr] StartX=40 StartY=-20 StartZ=0 EndX=80 EndY=-20 EndZ=0
    g6: LineSegment [constr] StartX=80 StartY=-20 StartZ=0 EndX=80 EndY=20 EndZ=0
    g7: LineSegment [constr] StartX=80 StartY=20 StartZ=0 EndX=40 EndY=20 EndZ=0
    g8: LineSegment [constr] StartX=-40 StartY=-20 StartZ=0 EndX=0 EndY=0 EndZ=0
    g9: LineSegment [constr] StartX=0 StartY=0 StartZ=0 EndX=40 EndY=-20 EndZ=0
    g10: LineSegment [constr] StartX=-40 StartY=44.5 StartZ=0 EndX=-40 EndY=-35.5 EndZ=0
    g11: LineSegment [constr] StartX=-40 StartY=-35.5 StartZ=0 EndX=40 EndY=-35.5 EndZ=0
    g12: LineSegment [constr] StartX=40 StartY=-35.5 StartZ=0 EndX=40 EndY=44.5 EndZ=0
    g13: LineSegment [constr] StartX=40 StartY=44.5 StartZ=0 EndX=-40 EndY=44.5 EndZ=0
    g14: ArcOfCircle [constr] CenterX=-33 CenterY=37.5 CenterZ=0 NormalX=0 NormalY=0 NormalZ=1 AngleXU=0 Radius=7 StartAngle=1.5708 EndAngle=3.14159
    g15: ArcOfCircle [constr] CenterX=33 CenterY=37.5 CenterZ=0 NormalX=0 NormalY=0 NormalZ=1 AngleXU=0 Radius=7 StartAngle=3e-16 EndAngle=1.5708
    g16: ArcOfCircle [constr] CenterX=33 CenterY=-28.5 CenterZ=0 NormalX=0 NormalY=0 NormalZ=1 AngleXU=0 Radius=7 StartAngle=4.71239 EndAngle=6.28319
    g17: ArcOfCircle [constr] CenterX=-33 CenterY=-28.5 CenterZ=0 NormalX=0 NormalY=0 NormalZ=1 AngleXU=0 Radius=7 StartAngle=3.14159 EndAngle=4.71239
    g18: Circle [constr] CenterX=-31.75 CenterY=36.25 CenterZ=0 NormalX=0 NormalY=0 NormalZ=1 AngleXU=0 Radius=3
    g19: Circle [constr] CenterX=31.75 CenterY=36.25 CenterZ=0 NormalX=0 NormalY=0 NormalZ=1 AngleXU=0 Radius=3
    g20: Circle [constr] CenterX=31.75 CenterY=-27.25 CenterZ=0 NormalX=0 NormalY=0 NormalZ=1 AngleXU=0 Radius=3
    g21: Circle [constr] CenterX=-31.75 CenterY=-27.25 CenterZ=0 NormalX=0 NormalY=0 NormalZ=1 AngleXU=0 Radius=3
    g22: LineSegment [constr] StartX=-40 StartY=-35.5 StartZ=0 EndX=-31.75 EndY=-27.25 EndZ=0
    g23: LineSegment [constr] StartX=31.75 StartY=-27.25 StartZ=0 EndX=40 EndY=-35.5 EndZ=0
    g24: LineSegment [constr] StartX=-40 StartY=44.5 StartZ=0 EndX=40 EndY=-35.5 EndZ=0
    g25: LineSegment [constr] StartX=-40 StartY=-35.5 StartZ=0 EndX=40 EndY=44.5 EndZ=0
    g26: Circle [constr] CenterX=-3.1e-15 CenterY=4.5 CenterZ=0 NormalX=0 NormalY=0 NormalZ=1 AngleXU=0 Radius=35
    g27: LineSegment [constr] StartX=-72.5 StartY=20.4 StartZ=0 EndX=-72.5 EndY=30.4 EndZ=0
    g28: LineSegment [constr] StartX=-72.5 StartY=30.4 StartZ=0 EndX=-40 EndY=44.5 EndZ=0
    g29: LineSegment [constr] StartX=-40 StartY=44.5 StartZ=0 EndX=40 EndY=44.5 EndZ=0
    g30: LineSegment [constr] StartX=40 StartY=44.5 StartZ=0 EndX=72.5 EndY=30.4 EndZ=0
    g31: LineSegment [constr] StartX=72.5 StartY=30.4 StartZ=0 EndX=72.5 EndY=20.4 EndZ=0
    g32: LineSegment [constr] StartX=72.5 StartY=20.4 StartZ=0 EndX=39.6 EndY=20.4 EndZ=0
    g33: LineSegment [constr] StartX=39.6 StartY=20.4 StartZ=0 EndX=39.6 EndY=-20.4 EndZ=0
    g34: LineSegment [constr] StartX=39.6 StartY=-20.4 StartZ=0 EndX=72.5 EndY=-20.4 EndZ=0
    g35: LineSegment [constr] StartX=72.5 StartY=-20.4 StartZ=0 EndX=72.5 EndY=-30.4 EndZ=0
    g36: LineSegment [constr] StartX=72.5 StartY=-30.4 StartZ=0 EndX=40 EndY=-35.5 EndZ=0
    g37: LineSegment [constr] StartX=40 StartY=-35.5 StartZ=0 EndX=-40 EndY=-35.5 EndZ=0
    g38: LineSegment [constr] StartX=-40 StartY=-35.5 StartZ=0 EndX=-72.5 EndY=-30.4 EndZ=0
    g39: LineSegment [constr] StartX=-72.5 StartY=-30.4 StartZ=0 EndX=-72.5 EndY=-20.4 EndZ=0
    g40: LineSegment [constr] StartX=-72.5 StartY=-20.4 StartZ=0 EndX=-39.6 EndY=-20.4 EndZ=0
    g41: LineSegment [constr] StartX=-39.6 StartY=-20.4 StartZ=0 EndX=-39.6 EndY=20.4 EndZ=0
    g42: LineSegment [constr] StartX=-39.6 StartY=20.4 StartZ=0 EndX=-72.5 EndY=20.4 EndZ=0
    g43: Circle [constr] CenterX=-3.1e-15 CenterY=4.5 CenterZ=0 NormalX=0 NormalY=0 NormalZ=1 AngleXU=0 Radius=35.4
    g44: LineSegment StartX=-25.8033 StartY=36.25 StartZ=0 EndX=-28.7766 EndY=41.4 EndZ=0
    g45: LineSegment StartX=-28.7766 StartY=41.4 StartZ=0 EndX=-34.7234 EndY=41.4 EndZ=0
    g46: LineSegment StartX=-34.7234 StartY=41.4 StartZ=0 EndX=-37.6967 EndY=36.25 EndZ=0
    g47: LineSegment StartX=-37.6967 StartY=36.25 StartZ=0 EndX=-34.7234 EndY=31.1 EndZ=0
    g48: LineSegment StartX=-34.7234 StartY=31.1 StartZ=0 EndX=-28.7766 EndY=31.1 EndZ=0
    g49: LineSegment StartX=-28.7766 StartY=31.1 StartZ=0 EndX=-25.8033 EndY=36.25 EndZ=0
    g50: Circle [constr] CenterX=-31.75 CenterY=36.25 CenterZ=0 NormalX=0 NormalY=0 NormalZ=1 AngleXU=0 Radius=5.94671
    g51: LineSegment StartX=34.7234 StartY=31.1 StartZ=0 EndX=37.6967 EndY=36.25 EndZ=0
    g52: LineSegment StartX=37.6967 StartY=36.25 StartZ=0 EndX=34.7234 EndY=41.4 EndZ=0
    g53: LineSegment StartX=34.7234 StartY=41.4 StartZ=0 EndX=28.7766 EndY=41.4 EndZ=0
    g54: LineSegment StartX=28.7766 StartY=41.4 StartZ=0 EndX=25.8033 EndY=36.25 EndZ=0
    g55: LineSegment StartX=25.8033 StartY=36.25 StartZ=0 EndX=28.7766 EndY=31.1 EndZ=0
    g56: LineSegment StartX=28.7766 StartY=31.1 StartZ=0 EndX=34.7234 EndY=31.1 EndZ=0
    g57: Circle [constr] CenterX=31.75 CenterY=36.25 CenterZ=0 NormalX=0 NormalY=0 NormalZ=1 AngleXU=0 Radius=5.94671
    g58: LineSegment StartX=28.7766 StartY=-32.4 StartZ=0 EndX=34.7234 EndY=-32.4 EndZ=0
    g59: LineSegment StartX=34.7234 StartY=-32.4 StartZ=0 EndX=37.6967 EndY=-27.25 EndZ=0
    g60: LineSegment StartX=37.6967 StartY=-27.25 StartZ=0 EndX=34.7234 EndY=-22.1 EndZ=0
    g61: LineSegment StartX=34.7234 StartY=-22.1 StartZ=0 EndX=28.7766 EndY=-22.1 EndZ=0
    g62: LineSegment StartX=28.7766 StartY=-22.1 StartZ=0 EndX=25.8033 EndY=-27.25 EndZ=0
    g63: LineSegment StartX=25.8033 StartY=-27.25 StartZ=0 EndX=28.7766 EndY=-32.4 EndZ=0
    g64: Circle [constr] CenterX=31.75 CenterY=-27.25 CenterZ=0 NormalX=0 NormalY=0 NormalZ=1 AngleXU=0 Radius=5.94671
    g65: LineSegment StartX=-28.7766 StartY=-32.4 StartZ=0 EndX=-25.8033 EndY=-27.25 EndZ=0
    g66: LineSegment StartX=-25.8033 StartY=-27.25 StartZ=0 EndX=-28.7766 EndY=-22.1 EndZ=0
    g67: LineSegment StartX=-28.7766 StartY=-22.1 StartZ=0 EndX=-34.7234 EndY=-22.1 EndZ=0
    g68: LineSegment StartX=-34.7234 StartY=-22.1 StartZ=0 EndX=-37.6967 EndY=-27.25 EndZ=0
    g69: LineSegment StartX=-37.6967 StartY=-27.25 StartZ=0 EndX=-34.7234 EndY=-32.4 EndZ=0
    g70: LineSegment StartX=-34.7234 StartY=-32.4 StartZ=0 EndX=-28.7766 EndY=-32.4 EndZ=0
    g71: Circle [constr] CenterX=-31.75 CenterY=-27.25 CenterZ=0 NormalX=0 NormalY=0 NormalZ=1 AngleXU=0 Radius=5.94671
  constraints (184):
    c: Coincident(g0,g1)
    c: Coincident(g1,g2)
    c: Coincident(g2,g3)
    c: Coincident(g3,g0)
    c: Vertical(g0)
    c: Vertical(g2)
    c: Horizontal(g1)
    c: Horizontal(g3)
    c: Coincident(g4,g5)
    c: Coincident(g5,g6)
    c: Coincident(g6,g7)
    c: Coincident(g7,g4)
    c: Vertical(g4)
    c: Vertical(g6)
    c: Horizontal(g5)
    c: Horizontal(g7)
    c: Equal(g3,g2)
    c: Equal(g2,g4)
    c: Equal(g4,g7)
    c: DistanceY(g0,g0) = 40
    c: DistanceX(g2,g4) = 80
    c: DistanceY(g2,g4) = 0
    c: Coincident(g8,g1)
    c: Coincident(g8,g-1)
    c: Coincident(g9,g8)
    c: Coincident(g9,g4)
    c: Equal(g9,g8)
    c: Coincident(g10,g11)
    c: Coincident(g11,g12)
    c: Coincident(g12,g13)
    c: Coincident(g13,g10)
    c: Vertical(g10)
    c: Vertical(g12)
    c: Horizontal(g11)
    c: Horizontal(g13)
    c: PointOnObject(g2,g10)
    c: PointOnObject(g4,g12)
    c: Equal(g13,g10)
    c: Equal(g16,g17)
    c: Equal(g17,g14)
    c: Equal(g14,g15)
    c: Diameter(g14) = 14
    c: Tangent(g14,g13) = -1.5708
    c: Tangent(g14,g10) = -1.5708
    c: Tangent(g15,g12) = -1.5708
    c: Tangent(g15,g13) = -1.5708
    c: Tangent(g17,g10) = -1.5708
    c: Tangent(g17,g11) = -1.5708
    c: Tangent(g16,g11) = -1.5708
    c: Tangent(g16,g12) = -1.5708
    c: Equal(g21,g20)
    c: Equal(g20,g19)
    c: Equal(g19,g18)
    c: Diameter(g18) = 6
    c: DistanceX(g18,g19) = 63.5
    c: DistanceY(g21,g18) = 63.5
    c: DistanceY(g21,g20) = 0
    c: DistanceY(g19,g18) = 0
    c: DistanceX(g18,g21) = 0
    c: DistanceX(g20,g19) = 0
    c: Coincident(g22,g10)
    c: Coincident(g22,g21)
    c: PointOnObject(g17,g22)
    c: Coincident(g23,g20)
    c: Coincident(g23,g11)
    c: PointOnObject(g16,g23)
    c: DistanceY(g2,g10) = 24.5
    c: DistanceY(g2) = 20
    c: Coincident(g24,g10)
    c: Coincident(g24,g11)
    c: Coincident(g25,g10)
    c: Coincident(g25,g12)
    c: Symmetric(g25,g25,g26)
    c: Diameter(g26) = 70
    c: Vertical(g27)
    c: Coincident(g27,g28)
    c: Coincident(g28,g10)
    c: Coincident(g28,g29)
    c: Coincident(g29,g12)
    c: Coincident(g29,g30)
    c: Coincident(g30,g31)
    c: Vertical(g31)
    c: Coincident(g31,g32)
    c: Horizontal(g32)
    c: Coincident(g32,g33)
    c: Vertical(g33)
    c: Coincident(g33,g34)
    c: Horizontal(g34)
    c: Coincident(g34,g35)
    c: Vertical(g35)
    c: Coincident(g35,g36)
    c: Coincident(g36,g11)
    c: Coincident(g36,g37)
    c: Coincident(g37,g10)
    c: Coincident(g10,g38)
    c: Coincident(g38,g39)
    c: Vertical(g39)
    c: Coincident(g39,g40)
    c: Horizontal(g40)
    c: Coincident(g40,g41)
    c: Vertical(g41)
    c: Coincident(g41,g42)
    c: Coincident(g42,g27)
    c: Horizontal(g42)
    c: DistanceX(g0,g27) = 7.5
    c: DistanceY(g0,g27) = 0.4
    c: DistanceX(g2,g41) = 0.4
    c: DistanceY(g40,g1) = 0.4
    c: Equal(g40,g42)
    c: Equal(g42,g34)
    c: Equal(g34,g32)
    c: DistanceY(g27,g27) = 10
    c: Equal(g27,g39)
    c: Equal(g39,g35)
    c: Equal(g35,g31)
    c: Equal(g33,g41)
    c: Equal(g30,g28)
    c: Equal(g36,g38)
    c: Coincident(g43,g26)
    c: Diameter(g43) = 70.8
    c: Coincident(g44,g45)
    c: Coincident(g45,g46)
    c: Coincident(g46,g47)
    c: Coincident(g47,g48)
    c: Coincident(g48,g49)
    c: Coincident(g49,g44)
    c: Equal(g44, g45-g49) x5
    c: PointOnObject(g44,g50)
    c: PointOnObject(g45,g50)
    c: PointOnObject(g46,g50)
    c: PointOnObject(g47,g50)
    c: PointOnObject(g48,g50)
    c: PointOnObject(g49,g50)
    c: Coincident(g50,g18)
    c: Distance(g45,g44) = 10.3
    c: Horizontal(g45)
    c: Coincident(g51,g52)
    c: Coincident(g52,g53)
    c: Coincident(g53,g54)
    c: Coincident(g54,g55)
    c: Coincident(g55,g56)
    c: Coincident(g56,g51)
    c: Equal(g51, g52-g56) x5
    c: PointOnObject(g51,g57)
    c: PointOnObject(g52,g57)
    c: PointOnObject(g53,g57)
    c: PointOnObject(g54,g57)
    c: PointOnObject(g55,g57)
    c: PointOnObject(g56,g57)
    c: Coincident(g57,g19)
    c: Coincident(g58,g59)
    c: Coincident(g59,g60)
    c: Coincident(g60,g61)
    c: Coincident(g61,g62)
    c: Coincident(g62,g63)
    c: Coincident(g63,g58)
    c: Equal(g58, g59-g63) x5
    c: PointOnObject(g58,g64)
    c: PointOnObject(g59,g64)
    c: PointOnObject(g60,g64)
    c: PointOnObject(g61,g64)
    c: PointOnObject(g62,g64)
    c: PointOnObject(g63,g64)
    c: Coincident(g64,g20)
    c: Coincident(g65,g66)
    c: Coincident(g66,g67)
    c: Coincident(g67,g68)
    c: Coincident(g68,g69)
    c: Coincident(g69,g70)
    c: Coincident(g70,g65)
    c: Equal(g65, g66-g70) x5
    c: PointOnObject(g65,g71)
    c: PointOnObject(g66,g71)
    c: PointOnObject(g67,g71)
    c: PointOnObject(g68,g71)
    c: PointOnObject(g69,g71)
    c: PointOnObject(g70,g71)
    c: Coincident(g71,g21)
    c: Equal(g71,g64)
    c: Equal(g64,g57)
    c: Equal(g57,g50)
    c: Horizontal(g53)
    c: Horizontal(g61)
    c: Horizontal(g67)
FEATURE [PartDesign::Pocket] Pocket004
  BaseFeature = -> Pocket003
  Direction = (0,1,-2e-16)
  Length = 6
  Length2 = 5
  Placement = pos=(0,0,0) rot=(1,0,0;1.5708rad)
  Profile = -> Sketch005
  ReferenceAxis = -> Sketch005 [N_Axis]
  Refine = true
  Suppressed = false
  Type = 0
FEATURE [PartDesign::Fillet] Fillet
  Base = -> Pocket004 [Edge31,Edge9,Edge39,Edge17,Edge42,Edge47,Edge20,Edge25]
  BaseFeature = -> Pocket004
  Placement = pos=(0,0,0) rot=(1,0,0;1.5708rad)
  Radius = 4
  Refine = true
  SupportTransform = false
  Suppressed = false
  UseAllEdges = false
FEATURE [PartDesign::Fillet] Fillet001
  Base = -> Fillet [Edge116,Edge110,Edge85,Edge82]
  BaseFeature = -> Fillet
  Placement = pos=(0,0,0) rot=(1,0,0;1.5708rad)
  Radius = 2
  Refine = true
  SupportTransform = false
  Suppressed = false
  UseAllEdges = false
FEATURE [PartDesign::Fillet] Fillet002
  Base = -> Fillet001 [Edge41,Edge70,Edge64,Edge68]
  BaseFeature = -> Fillet001
  Placement = pos=(0,0,0) rot=(1,0,0;1.5708rad)
  Radius = 18
  Refine = true
  SupportTransform = false
  Suppressed = false
  UseAllEdges = false
FEATURE [PartDesign::Fillet] Fillet003
  Base = -> Fillet002 [Edge58,Edge54,Edge43,Edge50]
  BaseFeature = -> Fillet002
  Placement = pos=(0,0,0) rot=(1,0,0;1.5708rad)
  Radius = 4
  Refine = true
  SupportTransform = false
  Suppressed = false
  UseAllEdges = false
FEATURE [Sketcher::SketchObject] Sketch006
  ArcFitTolerance = 1e-06
  AttachmentSupport = -> [Fillet003]
  FullyConstrained = true
  MakeInternals = false
  MapMode = 5
  Placement = pos=(72.5,0,0) rot=(0.707107,0,0.707107;3.14159rad)
  sketch-geometry (4):
    g0: LineSegment StartX=40.5 StartY=25 StartZ=0 EndX=44.5 EndY=21 EndZ=0
    g1: LineSegment StartX=44.5 StartY=21 StartZ=0 EndX=44.5 EndY=25 EndZ=0
    g2: LineSegment StartX=44.5 StartY=25 StartZ=0 EndX=40.5 EndY=25 EndZ=0
    g3: LineSegment [constr] StartX=44.5 StartY=25 StartZ=0 EndX=41.4 EndY=25 EndZ=0
  constraints (12):
    c: Coincident(g0,g1)
    c: Vertical(g1)
    c: Coincident(g1,g2)
    c: Coincident(g2,g0)
    c: Horizontal(g2)
    c: DistanceX(g1) = 44.5
    c: DistanceY(g1) = 25
    c: Coincident(g3,g1)
    c: Horizontal(g3)
    c: DistanceX(g3,g1) = 3.1
    c: DistanceY(g1,g1) = 4
    c: DistanceX(g2,g2) = 4
FEATURE [PartDesign::Pocket] Pocket005
  BaseFeature = -> Fillet003
  Direction = (-1,0,2e-16)
  Length = 5
  Length2 = 5
  Placement = pos=(0,0,0) rot=(1,0,0;1.5708rad)
  Profile = -> Sketch006
  ReferenceAxis = -> Sketch006 [N_Axis]
  Refine = true
  Suppressed = false
  Type = 1
FEATURE [PartDesign::Body] Body  label="surge_motor_mount_side"
  AllowCompound = false
  Group = -> [Sketch,Pad,Sketch001,Pocket,Sketch002,Pocket001,Sketch003,Pocket002,Sketch004,Pocket003,Sketch005,Pocket004,Fillet,Fillet001,Fillet002,Fillet003,Sketch006,Pocket005]
  Origin = -> Origin
  Tip = -> Pocket005
COMPONENT P20 — recipe-attached ("surge_motor_mount_top", a linked part whose construction recipe lives in a companion FreeCAD document of the same project; that document's serialized recipe follows).
Construction recipe (the companion document, serialized — sketch geometry with constraints, then the solid features built on it; lengths are millimeters unless a unit is written):

FCSTD DOCUMENT  (FreeCAD 1.0R39109 (Git))
Label: surge_motor_mount_top
License: All rights reserved
LicenseURL: https://en.wikipedia.org/wiki/All_rights_reserved
objects: Sketcher::SketchObject×3, PartDesign::Pocket×2, PartDesign::Fillet×2, PartDesign::Pad×1, PartDesign::Body×1
note: 22 computed .brp shape members not serialized (recipe doc carries the construction recipe); baked Part::Feature solids carry a one-line shape summary decoded from their .brp

FEATURE [Sketcher::SketchObject] Sketch
  ArcFitTolerance = 1e-06
  AttachmentSupport = -> [XZ_Plane]
  FullyConstrained = true
  MakeInternals = false
  MapMode = 5
  Placement = pos=(0,0,0) rot=(1,0,0;1.5708rad)
  sketch-geometry (30):
    g0: LineSegment [constr] StartX=-80 StartY=20 StartZ=0 EndX=-80 EndY=-20 EndZ=0
    g1: LineSegment [constr] StartX=-80 StartY=-20 StartZ=0 EndX=-40 EndY=-20 EndZ=0
    g2: LineSegment [constr] StartX=-40 StartY=-20 StartZ=0 EndX=-40 EndY=20 EndZ=0
    g3: LineSegment [constr] StartX=-40 StartY=20 StartZ=0 EndX=-80 EndY=20 EndZ=0
    g4: LineSegment [constr] StartX=40 StartY=20 StartZ=0 EndX=40 EndY=-20 EndZ=0
    g5: LineSegment [constr] StartX=40 StartY=-20 StartZ=0 EndX=80 EndY=-20 EndZ=0
    g6: LineSegment [constr] StartX=80 StartY=-20 StartZ=0 EndX=80 EndY=20 EndZ=0
    g7: LineSegment [constr] StartX=80 StartY=20 StartZ=0 EndX=40 EndY=20 EndZ=0
    g8: LineSegment [constr] StartX=-40 StartY=-20 StartZ=0 EndX=0 EndY=0 EndZ=0
    g9: LineSegment [constr] StartX=0 StartY=0 StartZ=0 EndX=40 EndY=-20 EndZ=0
    g10: LineSegment [constr] StartX=-40 StartY=44.5 StartZ=0 EndX=-40 EndY=-35.5 EndZ=0
    g11: LineSegment [constr] StartX=-40 StartY=-35.5 StartZ=0 EndX=40 EndY=-35.5 EndZ=0
    g12: LineSegment [constr] StartX=40 StartY=-35.5 StartZ=0 EndX=40 EndY=44.5 EndZ=0
    g13: LineSegment [constr] StartX=40 StartY=44.5 StartZ=0 EndX=-40 EndY=44.5 EndZ=0
    g14: ArcOfCircle [constr] CenterX=-40 CenterY=-35.5 CenterZ=0 NormalX=0 NormalY=0 NormalZ=1 AngleXU=0 Radius=14 StartAngle=0 EndAngle=1.5708
    g15: ArcOfCircle [constr] CenterX=-40 CenterY=44.5 CenterZ=0 NormalX=0 NormalY=0 NormalZ=1 AngleXU=0 Radius=14 StartAngle=4.71239 EndAngle=6.28319
    g16: ArcOfCircle [constr] CenterX=40 CenterY=-35.5 CenterZ=0 NormalX=0 NormalY=0 NormalZ=1 AngleXU=0 Radius=14 StartAngle=1.5708 EndAngle=3.14159
    g17: ArcOfCircle [constr] CenterX=40 CenterY=44.5 CenterZ=0 NormalX=0 NormalY=0 NormalZ=1 AngleXU=0 Radius=14 StartAngle=3.14159 EndAngle=4.71239
    g18: ArcOfCircle CenterX=-40.4 CenterY=44.9 CenterZ=0 NormalX=0 NormalY=0 NormalZ=1 AngleXU=0 Radius=14 StartAngle=4.71239 EndAngle=6.28319
    g19: ArcOfCircle CenterX=40.4 CenterY=44.9 CenterZ=0 NormalX=0 NormalY=0 NormalZ=1 AngleXU=0 Radius=14 StartAngle=3.14159 EndAngle=4.71239
    g20: LineSegment StartX=-40.4 StartY=20.4 StartZ=0 EndX=-72.5 EndY=20.4 EndZ=0
    g21: LineSegment StartX=-72.5 StartY=20.4 StartZ=0 EndX=-72.5 EndY=30.4 EndZ=0
    g22: LineSegment StartX=-72.5 StartY=30.4 StartZ=0 EndX=-26.4 EndY=49.9 EndZ=0
    g23: LineSegment StartX=-26.4 StartY=49.9 StartZ=0 EndX=26.4 EndY=49.9 EndZ=0
    g24: LineSegment StartX=26.4 StartY=49.9 StartZ=0 EndX=72.5 EndY=30.4 EndZ=0
    g25: LineSegment StartX=72.5 StartY=30.4 StartZ=0 EndX=72.5 EndY=20.4 EndZ=0
    g26: LineSegment StartX=72.5 StartY=20.4 StartZ=0 EndX=40.4 EndY=20.4 EndZ=0
    g27: LineSegment StartX=40.4 StartY=20.4 StartZ=0 EndX=40.4 EndY=30.9 EndZ=0
    g28: LineSegment StartX=-26.4 StartY=44.9 StartZ=0 EndX=26.4 EndY=44.9 EndZ=0
    g29: LineSegment StartX=-40.4 StartY=30.9 StartZ=0 EndX=-40.4 EndY=20.4 EndZ=0
  constraints (94):
    c: Coincident(g0,g1)
    c: Coincident(g1,g2)
    c: Coincident(g2,g3)
    c: Coincident(g3,g0)
    c: Vertical(g0)
    c: Vertical(g2)
    c: Horizontal(g1)
    c: Horizontal(g3)
    c: Coincident(g4,g5)
    c: Coincident(g5,g6)
    c: Coincident(g6,g7)
    c: Coincident(g7,g4)
    c: Vertical(g4)
    c: Vertical(g6)
    c: Horizontal(g5)
    c: Horizontal(g7)
    c: Equal(g3,g2)
    c: Equal(g2,g4)
    c: Equal(g4,g7)
    c: DistanceY(g0,g0) = 40
    c: DistanceX(g2,g4) = 80
    c: DistanceY(g2,g4) = 0
    c: Coincident(g8,g1)
    c: Coincident(g8,g-1)
    c: Coincident(g9,g8)
    c: Coincident(g9,g4)
    c: Equal(g9,g8)
    c: Coincident(g10,g11)
    c: Coincident(g11,g12)
    c: Coincident(g12,g13)
    c: Coincident(g13,g10)
    c: Vertical(g10)
    c: Vertical(g12)
    c: Horizontal(g11)
    c: Horizontal(g13)
    c: PointOnObject(g2,g10)
    c: PointOnObject(g4,g12)
    c: Equal(g13,g10)
    c: DistanceY(g2,g10) = 24.5
    c: DistanceY(g2) = 20
    c: Coincident(g14,g10)
    c: PointOnObject(g14,g10)
    c: PointOnObject(g14,g11)
    c: Diameter(g14) = 28
    c: Coincident(g15,g10)
    c: PointOnObject(g15,g13)
    c: PointOnObject(g15,g10)
    c: Coincident(g16,g11)
    c: PointOnObject(g16,g11)
    c: PointOnObject(g16,g12)
    c: Coincident(g17,g12)
    c: PointOnObject(g17,g13)
    c: PointOnObject(g17,g12)
    c: Equal(g14,g16)
    c: Equal(g16,g17)
    c: Equal(g17,g15)
    c: Horizontal(g20)
    c: Coincident(g20,g21)
    c: Vertical(g21)
    c: Coincident(g21,g22)
    c: Coincident(g22,g23)
    c: Horizontal(g23)
    c: Coincident(g23,g24)
    c: Coincident(g24,g25)
    c: Vertical(g25)
    c: Coincident(g25,g26)
    c: Horizontal(g26)
    c: Coincident(g26,g27)
    c: Coincident(g27,g19)
    c: Vertical(g27)
    c: Coincident(g28,g18)
    c: Coincident(g28,g19)
    c: Horizontal(g28)
    c: Coincident(g29,g18)
    c: Coincident(g29,g20)
    c: Vertical(g29)
    c: DistanceX(g0,g20) = 7.5
    c: DistanceY(g0,g20) = 0.4
    c: DistanceX(g20,g2) = 0.4
    c: Perpendicular(g18,g29)
    c: DistanceY(g15,g18) = 0.4
    c: Perpendicular(g18,g28)
    c: DistanceY(g18,g22) = 5
    c: DistanceX(g18,g22) = 0
    c: DistanceY(g20,g21) = 10
    c: Equal(g20,g26)
    c: Equal(g21,g25)
    c: Equal(g22,g24)
    c: DistanceX(g4,g26) = 0.4
    c: DistanceY(g4,g26) = 0.4
    c: Equal(g27,g29)
    c: Perpendicular(g19,g27)
    c: Perpendicular(g19,g28)
    c: DistanceY(g15,g18) = 0.4
FEATURE [PartDesign::Pad] Pad
  Direction = (0,-1,2e-16)
  Length = 25
  Length2 = 10
  Placement = pos=(0,0,0) rot=(1,0,0;1.5708rad)
  Profile = -> Sketch
  ReferenceAxis = -> Sketch [N_Axis]
  Refine = true
  Suppressed = false
  Type = 0
FEATURE [Sketcher::SketchObject] Sketch001
  ArcFitTolerance = 1e-06
  AttachmentSupport = -> [Pad]
  FullyConstrained = true
  MakeInternals = false
  MapMode = 5
  Placement = pos=(0,4.5e-15,20.4) rot=(1,0,0;3.14159rad)
  sketch-geometry (14):
    g0: LineSegment [constr] StartX=-72.5 StartY=0 StartZ=0 EndX=-47.5 EndY=0 EndZ=0
    g1: LineSegment [constr] StartX=-47.5 StartY=0 StartZ=0 EndX=-47.5 EndY=25 EndZ=0
    g2: LineSegment [constr] StartX=-47.5 StartY=25 StartZ=0 EndX=-72.5 EndY=25 EndZ=0
    g3: LineSegment [constr] StartX=-72.5 StartY=25 StartZ=0 EndX=-72.5 EndY=0 EndZ=0
    g4: LineSegment [constr] StartX=72.5 StartY=0 StartZ=0 EndX=72.5 EndY=25 EndZ=0
    g5: LineSegment [constr] StartX=72.5 StartY=25 StartZ=0 EndX=47.5 EndY=25 EndZ=0
    g6: LineSegment [constr] StartX=47.5 StartY=25 StartZ=0 EndX=47.5 EndY=0 EndZ=0
    g7: LineSegment [constr] StartX=47.5 StartY=0 StartZ=0 EndX=72.5 EndY=0 EndZ=0
    g8: LineSegment [constr] StartX=-72.5 StartY=25 StartZ=0 EndX=-47.5 EndY=0 EndZ=0
    g9: LineSegment [constr] StartX=-72.5 StartY=0 StartZ=0 EndX=-47.5 EndY=25 EndZ=0
    g10: LineSegment [constr] StartX=47.5 StartY=25 StartZ=0 EndX=72.5 EndY=0 EndZ=0
    g11: LineSegment [constr] StartX=47.5 StartY=0 StartZ=0 EndX=72.5 EndY=25 EndZ=0
    g12: Circle CenterX=-60 CenterY=12.5 CenterZ=0 NormalX=0 NormalY=0 NormalZ=1 AngleXU=0 Radius=4.3
    g13: Circle CenterX=60 CenterY=12.5 CenterZ=0 NormalX=0 NormalY=0 NormalZ=1 AngleXU=0 Radius=4.3
  constraints (36):
    c: Coincident(g0,g1)
    c: Coincident(g1,g2)
    c: Coincident(g2,g3)
    c: Coincident(g3,g0)
    c: Horizontal(g0)
    c: Horizontal(g2)
    c: Vertical(g1)
    c: Vertical(g3)
    c: Distance(g1,g3) = 25
    c: Distance(g0,g2) = 25
    c: PointOnObject(g0,g-1)
    c: DistanceX(g0) = -47.5
    c: Coincident(g4,g5)
    c: Coincident(g5,g6)
    c: Coincident(g6,g7)
    c: Coincident(g7,g4)
    c: Vertical(g4)
    c: Vertical(g6)
    c: Horizontal(g5)
    c: Horizontal(g7)
    c: PointOnObject(g4,g-1)
    c: Equal(g6,g5)
    c: Equal(g5,g1)
    c: DistanceX(g6) = 47.5
    c: Coincident(g8,g2)
    c: Coincident(g8,g0)
    c: Coincident(g9,g0)
    c: Coincident(g9,g1)
    c: Coincident(g10,g5)
    c: Coincident(g10,g4)
    c: Coincident(g11,g6)
    c: Coincident(g11,g4)
    c: Diameter(g12) = 8.6
    c: Symmetric(g8,g8,g12)
    c: Symmetric(g11,g11,g13)
    c: Equal(g13,g12)
FEATURE [PartDesign::Pocket] Pocket
  BaseFeature = -> Pad
  Direction = (0,0,1)
  Length = 5
  Length2 = 5
  Placement = pos=(0,0,0) rot=(1,0,0;1.5708rad)
  Profile = -> Sketch001
  ReferenceAxis = -> Sketch001 [N_Axis]
  Refine = true
  Suppressed = false
  Type = 1
FEATURE [Sketcher::SketchObject] Sketch002
  ArcFitTolerance = 1e-06
  AttachmentOffset = pos=(0,0,-5) rot=(0,0,1;0rad)
  AttachmentSupport = -> [Pocket]
  FullyConstrained = true
  MakeInternals = false
  MapMode = 5
  Placement = pos=(0,4.5e-15,25.4) rot=(1,0,0;3.14159rad)
  expr: Constraints[11] = Sketch001.Constraints[11]
  expr: Constraints[23] = Sketch001.Constraints[23]
  expr: Constraints[32] = Sketch001.Constraints[32]
  expr: Constraints[8] = Sketch001.Constraints[8]
  expr: Constraints[9] = Sketch001.Constraints[9]
  sketch-geometry (16):
    g0: LineSegment [constr] StartX=-72.5 StartY=0 StartZ=0 EndX=-47.5 EndY=0 EndZ=0
    g1: LineSegment [constr] StartX=-47.5 StartY=0 StartZ=0 EndX=-47.5 EndY=25 EndZ=0
    g2: LineSegment [constr] StartX=-47.5 StartY=25 StartZ=0 EndX=-72.5 EndY=25 EndZ=0
    g3: LineSegment [constr] StartX=-72.5 StartY=25 StartZ=0 EndX=-72.5 EndY=0 EndZ=0
    g4: LineSegment [constr] StartX=72.5 StartY=0 StartZ=0 EndX=72.5 EndY=25 EndZ=0
    g5: LineSegment [constr] StartX=72.5 StartY=25 StartZ=0 EndX=47.5 EndY=25 EndZ=0
    g6: LineSegment [constr] StartX=47.5 StartY=25 StartZ=0 EndX=47.5 EndY=0 EndZ=0
    g7: LineSegment [constr] StartX=47.5 StartY=0 StartZ=0 EndX=72.5 EndY=0 EndZ=0
    g8: LineSegment [constr] StartX=-72.5 StartY=25 StartZ=0 EndX=-47.5 EndY=0 EndZ=0
    g9: LineSegment [constr] StartX=-72.5 StartY=0 StartZ=0 EndX=-47.5 EndY=25 EndZ=0
    g10: LineSegment [constr] StartX=47.5 StartY=25 StartZ=0 EndX=72.5 EndY=0 EndZ=0
    g11: LineSegment [constr] StartX=47.5 StartY=0 StartZ=0 EndX=72.5 EndY=25 EndZ=0
    g12: Circle [constr] CenterX=-60 CenterY=12.5 CenterZ=0 NormalX=0 NormalY=0 NormalZ=1 AngleXU=0 Radius=4.3
    g13: Circle [constr] CenterX=60 CenterY=12.5 CenterZ=0 NormalX=0 NormalY=0 NormalZ=1 AngleXU=0 Radius=4.3
    g14: Circle CenterX=-60 CenterY=12.5 CenterZ=0 NormalX=0 NormalY=0 NormalZ=1 AngleXU=0 Radius=6.75
    g15: Circle CenterX=60 CenterY=12.5 CenterZ=0 NormalX=0 NormalY=0 NormalZ=1 AngleXU=0 Radius=6.75
  constraints (40):
    c: Coincident(g0,g1)
    c: Coincident(g1,g2)
    c: Coincident(g2,g3)
    c: Coincident(g3,g0)
    c: Horizontal(g0)
    c: Horizontal(g2)
    c: Vertical(g1)
    c: Vertical(g3)
    c: Distance(g1,g3) = 25
    c: Distance(g0,g2) = 25
    c: PointOnObject(g0,g-1)
    c: DistanceX(g0) = -47.5
    c: Coincident(g4,g5)
    c: Coincident(g5,g6)
    c: Coincident(g6,g7)
    c: Coincident(g7,g4)
    c: Vertical(g4)
    c: Vertical(g6)
    c: Horizontal(g5)
    c: Horizontal(g7)
    c: PointOnObject(g4,g-1)
    c: Equal(g6,g5)
    c: Equal(g5,g1)
    c: DistanceX(g6) = 47.5
    c: Coincident(g8,g2)
    c: Coincident(g8,g0)
    c: Coincident(g9,g0)
    c: Coincident(g9,g1)
    c: Coincident(g10,g5)
    c: Coincident(g10,g4)
    c: Coincident(g11,g6)
    c: Coincident(g11,g4)
    c: Diameter(g12) = 8.6
    c: Symmetric(g8,g8,g12)
    c: Symmetric(g11,g11,g13)
    c: Equal(g13,g12)
    c: Coincident(g14,g12)
    c: Coincident(g15,g13)
    c: Equal(g14,g15)
    c: Diameter(g14) = 13.5
FEATURE [PartDesign::Pocket] Pocket001
  BaseFeature = -> Pocket
  Direction = (0,0,1)
  Length = 5
  Length2 = 5
  Placement = pos=(0,0,0) rot=(1,0,0;1.5708rad)
  Profile = -> Sketch002
  ReferenceAxis = -> Sketch002 [N_Axis]
  Refine = true
  Suppressed = false
  Type = 1
FEATURE [PartDesign::Fillet] Fillet
  Base = -> Pocket001 [Edge27,Edge18,Edge23,Edge14]
  BaseFeature = -> Pocket001
  Placement = pos=(0,0,0) rot=(1,0,0;1.5708rad)
  Radius = 4
  Refine = true
  SupportTransform = false
  Suppressed = false
  UseAllEdges = false
FEATURE [PartDesign::Fillet] Fillet001
  Base = -> Fillet [Edge30,Edge23]
  BaseFeature = -> Fillet
  Placement = pos=(0,0,0) rot=(1,0,0;1.5708rad)
  Radius = 18
  Refine = true
  SupportTransform = false
  Suppressed = false
  UseAllEdges = false
FEATURE [PartDesign::Body] Body  label="surge_motor_mount_top"
  AllowCompound = false
  Group = -> [Sketch,Pad,Sketch001,Pocket,Sketch002,Pocket001,Fillet,Fillet001]
  Origin = -> Origin
  Tip = -> Fillet001
PROVENANCE & LICENSES
A FreeCAD (.FCStd) document from a public repository crawl; recipes are the document's own serialized feature recipes (and, for linked parts, companion documents' recipes).
License: as declared in the source repository (recorded in the dataset sidecar).
